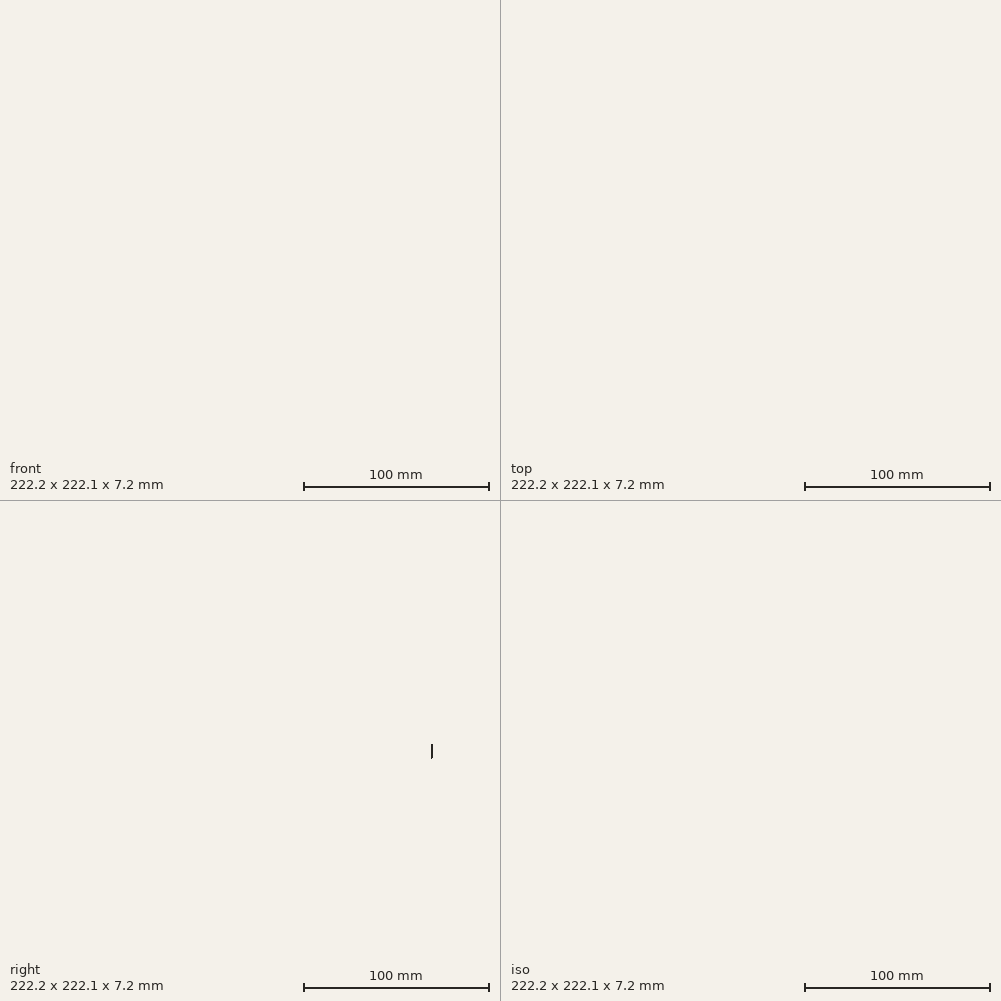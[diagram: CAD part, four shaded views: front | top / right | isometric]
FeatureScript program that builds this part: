
annotation { "Feature Type Name" : "Feature", "Feature Type Description" : "" }
export const myFeature = defineFeature(function(context is Context, id is Id, definition is map)
    precondition{}
    {
        {
            var Q0;
            Q0=qCreatedBy(makeId("Top.planeOp"),FACE);
            var sketch = newSketch(context, id + "F0", { "sketchPlane" : qUnion([Q0])});
            skCircle(sketch, "E0", {"center": v(0, 0) * mm, "radius": 101.6 * mm});
            skCircle(sketch, "E1", {"center": v(0, 0) * mm, "radius": 111.13 * mm});
            skSolve(sketch);
        }
        {
            var Q0;
            Q0=qSketchRegion(id+"F0",true);
            extrude(context, id + "F1", {"entities" : qUnion([Q0]), "depth" : 12.7 * mm});
        }
        {
            var Q0;
            Q0=makeQuery(id+"F1.opExtrude","CAP_FACE",FACE,{"disambiguationData":[OSD([sQuery(id+"F0.wireOp",EDGE,"E0"),sQuery(id+"F0.wireOp",EDGE,"E1")])],"isStart":false});
            var sketch = newSketch(context, id + "F2", { "sketchPlane" : qUnion([Q0])});
            skLineSegment(sketch, "E2", {"start": v(0, 0) * mm, "end": v(0, 111.13) * mm, "construction": true});
            skArc(sketch, "E3", {"start": v(1.28, 110.4) * mm, "mid": v(0.74, 110.93) * mm, "end": v(0, 111.12) * mm});
            skCircle(sketch, "E4", {"center": v(0, 0) * mm, "radius": 109.64 * mm, "construction": true});
            skArc(sketch, "E5", {"start": v(5.38, 111) * mm, "mid": v(4.64, 110.84) * mm, "end": v(4.08, 110.34) * mm});
            skArc(sketch, "E6", {"start": v(1.28, 110.4) * mm, "mid": v(2.66, 109.6) * mm, "end": v(4.08, 110.34) * mm});
            skLineSegment(sketch, "E7", {"start": v(5.31, 109.5) * mm, "end": v(5.38, 111) * mm, "construction": true});
            skCircle(sketch, "E8", {"center": v(0, 0) * mm, "radius": 129.3 * mm});
            skArc(sketch, "E9.1.0", {"start": v(-4.05, 110.33) * mm, "mid": v(-4.62, 110.84) * mm, "end": v(-5.37, 111) * mm});
            skArc(sketch, "E9.1.1", {"start": v(0.01, 111.12) * mm, "mid": v(-0.72, 110.93) * mm, "end": v(-1.26, 110.4) * mm});
            skArc(sketch, "E9.1.2", {"start": v(-4.05, 110.33) * mm, "mid": v(-2.64, 109.6) * mm, "end": v(-1.26, 110.4) * mm});
            skArc(sketch, "E9.2.0", {"start": v(-9.38, 110.01) * mm, "mid": v(-9.97, 110.48) * mm, "end": v(-10.73, 110.6) * mm});
            skArc(sketch, "E9.2.1", {"start": v(-5.35, 111) * mm, "mid": v(-6.08, 110.77) * mm, "end": v(-6.6, 110.22) * mm});
            skArc(sketch, "E9.2.2", {"start": v(-9.38, 110.01) * mm, "mid": v(-7.93, 109.35) * mm, "end": v(-6.6, 110.22) * mm});
            skArc(sketch, "E9.3.0", {"start": v(-14.68, 109.43) * mm, "mid": v(-15.3, 109.87) * mm, "end": v(-16.06, 109.96) * mm});
            skArc(sketch, "E9.3.1", {"start": v(-10.71, 110.6) * mm, "mid": v(-11.42, 110.35) * mm, "end": v(-11.9, 109.77) * mm});
            skArc(sketch, "E9.3.2", {"start": v(-14.68, 109.43) * mm, "mid": v(-13.2, 108.84) * mm, "end": v(-11.9, 109.77) * mm});
            skArc(sketch, "E9.4.0", {"start": v(-19.95, 108.6) * mm, "mid": v(-20.59, 109) * mm, "end": v(-21.35, 109.05) * mm});
            skArc(sketch, "E9.4.1", {"start": v(-16.04, 109.96) * mm, "mid": v(-16.74, 109.66) * mm, "end": v(-17.2, 109.06) * mm});
            skArc(sketch, "E9.4.2", {"start": v(-19.95, 108.6) * mm, "mid": v(-18.45, 108.07) * mm, "end": v(-17.2, 109.06) * mm});
            skArc(sketch, "E9.5.0", {"start": v(-25.17, 107.5) * mm, "mid": v(-25.83, 107.88) * mm, "end": v(-26.6, 107.9) * mm});
            skArc(sketch, "E9.5.1", {"start": v(-21.34, 109.06) * mm, "mid": v(-22.02, 108.73) * mm, "end": v(-22.45, 108.1) * mm});
            skArc(sketch, "E9.5.2", {"start": v(-25.17, 107.5) * mm, "mid": v(-23.65, 107.06) * mm, "end": v(-22.45, 108.1) * mm});
            skArc(sketch, "E9.6.0", {"start": v(-30.34, 106.16) * mm, "mid": v(-31.01, 106.51) * mm, "end": v(-31.78, 106.49) * mm});
            skArc(sketch, "E9.6.1", {"start": v(-26.58, 107.9) * mm, "mid": v(-27.24, 107.54) * mm, "end": v(-27.65, 106.9) * mm});
            skArc(sketch, "E9.6.2", {"start": v(-30.34, 106.16) * mm, "mid": v(-28.79, 105.79) * mm, "end": v(-27.65, 106.9) * mm});
            skArc(sketch, "E9.7.0", {"start": v(-35.43, 104.57) * mm, "mid": v(-36.12, 104.89) * mm, "end": v(-36.88, 104.83) * mm});
            skArc(sketch, "E9.7.1", {"start": v(-31.76, 106.49) * mm, "mid": v(-32.4, 106.1) * mm, "end": v(-32.78, 105.44) * mm});
            skArc(sketch, "E9.7.2", {"start": v(-35.43, 104.57) * mm, "mid": v(-33.87, 104.28) * mm, "end": v(-32.78, 105.44) * mm});
            skArc(sketch, "E9.8.0", {"start": v(-40.44, 102.74) * mm, "mid": v(-41.15, 103.02) * mm, "end": v(-41.9, 102.92) * mm});
            skArc(sketch, "E9.8.1", {"start": v(-36.87, 104.83) * mm, "mid": v(-37.5, 104.4) * mm, "end": v(-37.83, 103.73) * mm});
            skArc(sketch, "E9.8.2", {"start": v(-40.44, 102.74) * mm, "mid": v(-38.87, 102.52) * mm, "end": v(-37.83, 103.73) * mm});
            skArc(sketch, "E9.9.0", {"start": v(-45.36, 100.66) * mm, "mid": v(-46.08, 100.91) * mm, "end": v(-46.83, 100.78) * mm});
            skArc(sketch, "E9.9.1", {"start": v(-41.9, 102.93) * mm, "mid": v(-42.5, 102.47) * mm, "end": v(-42.8, 101.78) * mm});
            skArc(sketch, "E9.9.2", {"start": v(-45.36, 100.66) * mm, "mid": v(-43.77, 100.52) * mm, "end": v(-42.8, 101.78) * mm});
            skArc(sketch, "E9.10.0", {"start": v(-50.17, 98.35) * mm, "mid": v(-50.9, 98.57) * mm, "end": v(-51.64, 98.4) * mm});
            skArc(sketch, "E9.10.1", {"start": v(-46.82, 100.78) * mm, "mid": v(-47.4, 100.3) * mm, "end": v(-47.67, 99.6) * mm});
            skArc(sketch, "E9.10.2", {"start": v(-50.17, 98.35) * mm, "mid": v(-48.58, 98.29) * mm, "end": v(-47.67, 99.6) * mm});
            skArc(sketch, "E9.11.0", {"start": v(-54.86, 95.81) * mm, "mid": v(-55.6, 96) * mm, "end": v(-56.34, 95.79) * mm});
            skArc(sketch, "E9.11.1", {"start": v(-51.63, 98.4) * mm, "mid": v(-52.19, 97.9) * mm, "end": v(-52.42, 97.17) * mm});
            skArc(sketch, "E9.11.2", {"start": v(-54.86, 95.81) * mm, "mid": v(-53.27, 95.83) * mm, "end": v(-52.42, 97.17) * mm});
            skArc(sketch, "E9.12.0", {"start": v(-59.43, 93.05) * mm, "mid": v(-60.18, 93.2) * mm, "end": v(-60.9, 92.95) * mm});
            skArc(sketch, "E9.12.1", {"start": v(-56.32, 95.8) * mm, "mid": v(-56.86, 95.26) * mm, "end": v(-57.06, 94.53) * mm});
            skArc(sketch, "E9.12.2", {"start": v(-59.43, 93.05) * mm, "mid": v(-57.84, 93.14) * mm, "end": v(-57.06, 94.53) * mm});
            skArc(sketch, "E9.13.0", {"start": v(-63.85, 90.07) * mm, "mid": v(-64.6, 90.18) * mm, "end": v(-65.32, 89.9) * mm});
            skArc(sketch, "E9.13.1", {"start": v(-60.89, 92.96) * mm, "mid": v(-61.4, 92.4) * mm, "end": v(-61.56, 91.66) * mm});
            skArc(sketch, "E9.13.2", {"start": v(-63.85, 90.07) * mm, "mid": v(-62.27, 90.24) * mm, "end": v(-61.56, 91.66) * mm});
            skArc(sketch, "E9.14.0", {"start": v(-68.13, 86.88) * mm, "mid": v(-68.89, 86.95) * mm, "end": v(-69.58, 86.64) * mm});
            skArc(sketch, "E9.14.1", {"start": v(-65.3, 89.91) * mm, "mid": v(-65.79, 89.32) * mm, "end": v(-65.91, 88.58) * mm});
            skArc(sketch, "E9.14.2", {"start": v(-68.13, 86.88) * mm, "mid": v(-66.56, 87.12) * mm, "end": v(-65.91, 88.58) * mm});
            skArc(sketch, "E9.15.0", {"start": v(-72.25, 83.49) * mm, "mid": v(-73, 83.52) * mm, "end": v(-73.69, 83.18) * mm});
            skArc(sketch, "E9.15.1", {"start": v(-69.57, 86.65) * mm, "mid": v(-70.02, 86.04) * mm, "end": v(-70.12, 85.3) * mm});
            skArc(sketch, "E9.15.2", {"start": v(-72.25, 83.49) * mm, "mid": v(-70.69, 83.8) * mm, "end": v(-70.12, 85.3) * mm});
            skArc(sketch, "E9.16.0", {"start": v(-76.2, 79.9) * mm, "mid": v(-76.96, 79.9) * mm, "end": v(-77.62, 79.52) * mm});
            skArc(sketch, "E9.16.1", {"start": v(-73.68, 83.19) * mm, "mid": v(-74.1, 82.56) * mm, "end": v(-74.16, 81.8) * mm});
            skArc(sketch, "E9.16.2", {"start": v(-76.2, 79.9) * mm, "mid": v(-74.65, 80.3) * mm, "end": v(-74.16, 81.8) * mm});
            skArc(sketch, "E9.17.0", {"start": v(-79.97, 76.13) * mm, "mid": v(-80.73, 76.09) * mm, "end": v(-81.37, 75.68) * mm});
            skArc(sketch, "E9.17.1", {"start": v(-77.61, 79.53) * mm, "mid": v(-78, 78.88) * mm, "end": v(-78.02, 78.13) * mm});
            skArc(sketch, "E9.17.2", {"start": v(-79.97, 76.13) * mm, "mid": v(-78.45, 76.6) * mm, "end": v(-78.02, 78.13) * mm});
            skArc(sketch, "E9.18.0", {"start": v(-83.55, 72.17) * mm, "mid": v(-84.31, 72.1) * mm, "end": v(-84.93, 71.66) * mm});
            skArc(sketch, "E9.18.1", {"start": v(-81.36, 75.69) * mm, "mid": v(-81.72, 75.02) * mm, "end": v(-81.7, 74.27) * mm});
            skArc(sketch, "E9.18.2", {"start": v(-83.55, 72.17) * mm, "mid": v(-82.06, 72.71) * mm, "end": v(-81.7, 74.27) * mm});
            skArc(sketch, "E9.19.0", {"start": v(-86.94, 68.05) * mm, "mid": v(-87.7, 67.94) * mm, "end": v(-88.3, 67.47) * mm});
            skArc(sketch, "E9.19.1", {"start": v(-84.93, 71.67) * mm, "mid": v(-85.25, 70.99) * mm, "end": v(-85.2, 70.23) * mm});
            skArc(sketch, "E9.19.2", {"start": v(-86.94, 68.05) * mm, "mid": v(-85.47, 68.66) * mm, "end": v(-85.2, 70.23) * mm});
            skArc(sketch, "E9.20.0", {"start": v(-90.13, 63.77) * mm, "mid": v(-90.88, 63.62) * mm, "end": v(-91.45, 63.13) * mm});
            skArc(sketch, "E9.20.1", {"start": v(-88.29, 67.48) * mm, "mid": v(-88.58, 66.78) * mm, "end": v(-88.5, 66.03) * mm});
            skArc(sketch, "E9.20.2", {"start": v(-90.13, 63.77) * mm, "mid": v(-88.7, 64.45) * mm, "end": v(-88.5, 66.03) * mm});
            skArc(sketch, "E9.21.0", {"start": v(-93.1, 59.34) * mm, "mid": v(-93.84, 59.16) * mm, "end": v(-94.4, 58.63) * mm});
            skArc(sketch, "E9.21.1", {"start": v(-91.45, 63.14) * mm, "mid": v(-91.7, 62.43) * mm, "end": v(-91.58, 61.68) * mm});
            skArc(sketch, "E9.21.2", {"start": v(-93.1, 59.34) * mm, "mid": v(-91.7, 60.1) * mm, "end": v(-91.58, 61.68) * mm});
            skArc(sketch, "E9.22.0", {"start": v(-95.86, 54.78) * mm, "mid": v(-96.6, 54.56) * mm, "end": v(-97.12, 54) * mm});
            skArc(sketch, "E9.22.1", {"start": v(-94.39, 58.65) * mm, "mid": v(-94.61, 57.92) * mm, "end": v(-94.45, 57.18) * mm});
            skArc(sketch, "E9.22.2", {"start": v(-95.86, 54.78) * mm, "mid": v(-94.5, 55.6) * mm, "end": v(-94.45, 57.18) * mm});
            skArc(sketch, "E9.23.0", {"start": v(-98.4, 50.08) * mm, "mid": v(-99.12, 49.82) * mm, "end": v(-99.62, 49.25) * mm});
            skArc(sketch, "E9.23.1", {"start": v(-97.11, 54.02) * mm, "mid": v(-97.3, 53.28) * mm, "end": v(-97.1, 52.55) * mm});
            skArc(sketch, "E9.23.2", {"start": v(-98.4, 50.08) * mm, "mid": v(-97.07, 50.96) * mm, "end": v(-97.1, 52.55) * mm});
            skArc(sketch, "E9.24.0", {"start": v(-100.7, 45.27) * mm, "mid": v(-101.4, 44.98) * mm, "end": v(-101.88, 44.38) * mm});
            skArc(sketch, "E9.24.1", {"start": v(-99.6, 49.26) * mm, "mid": v(-99.76, 48.52) * mm, "end": v(-99.53, 47.8) * mm});
            skArc(sketch, "E9.24.2", {"start": v(-100.7, 45.27) * mm, "mid": v(-99.42, 46.21) * mm, "end": v(-99.53, 47.8) * mm});
            skArc(sketch, "E9.25.0", {"start": v(-102.77, 40.35) * mm, "mid": v(-103.46, 40.03) * mm, "end": v(-103.9, 39.4) * mm});
            skArc(sketch, "E9.25.1", {"start": v(-101.87, 44.4) * mm, "mid": v(-101.99, 43.64) * mm, "end": v(-101.72, 42.94) * mm});
            skArc(sketch, "E9.25.2", {"start": v(-102.77, 40.35) * mm, "mid": v(-101.54, 41.36) * mm, "end": v(-101.72, 42.94) * mm});
            skArc(sketch, "E9.26.0", {"start": v(-104.6, 35.34) * mm, "mid": v(-105.27, 34.98) * mm, "end": v(-105.69, 34.34) * mm});
            skArc(sketch, "E9.26.1", {"start": v(-103.9, 39.42) * mm, "mid": v(-103.98, 38.67) * mm, "end": v(-103.68, 37.97) * mm});
            skArc(sketch, "E9.26.2", {"start": v(-104.6, 35.34) * mm, "mid": v(-103.42, 36.4) * mm, "end": v(-103.68, 37.97) * mm});
            skArc(sketch, "E9.27.0", {"start": v(-106.19, 30.24) * mm, "mid": v(-106.84, 29.85) * mm, "end": v(-107.22, 29.2) * mm});
            skArc(sketch, "E9.27.1", {"start": v(-105.68, 34.35) * mm, "mid": v(-105.72, 33.6) * mm, "end": v(-105.4, 32.92) * mm});
            skArc(sketch, "E9.27.2", {"start": v(-106.19, 30.24) * mm, "mid": v(-105.06, 31.36) * mm, "end": v(-105.4, 32.92) * mm});
            skArc(sketch, "E9.28.0", {"start": v(-107.52, 25.08) * mm, "mid": v(-108.16, 24.66) * mm, "end": v(-108.5, 23.98) * mm});
            skArc(sketch, "E9.28.1", {"start": v(-107.22, 29.2) * mm, "mid": v(-107.22, 28.45) * mm, "end": v(-106.86, 27.79) * mm});
            skArc(sketch, "E9.28.2", {"start": v(-107.52, 25.08) * mm, "mid": v(-106.45, 26.25) * mm, "end": v(-106.86, 27.79) * mm});
            skArc(sketch, "E9.29.0", {"start": v(-108.6, 19.85) * mm, "mid": v(-109.22, 19.4) * mm, "end": v(-109.54, 18.7) * mm});
            skArc(sketch, "E9.29.1", {"start": v(-108.5, 24) * mm, "mid": v(-108.47, 23.24) * mm, "end": v(-108.08, 22.6) * mm});
            skArc(sketch, "E9.29.2", {"start": v(-108.6, 19.85) * mm, "mid": v(-107.6, 21.08) * mm, "end": v(-108.08, 22.6) * mm});
            skArc(sketch, "E9.30.0", {"start": v(-109.44, 14.58) * mm, "mid": v(-110.03, 14.1) * mm, "end": v(-110.31, 13.4) * mm});
            skArc(sketch, "E9.30.1", {"start": v(-109.54, 18.72) * mm, "mid": v(-109.47, 17.97) * mm, "end": v(-109.04, 17.35) * mm});
            skArc(sketch, "E9.30.2", {"start": v(-109.44, 14.58) * mm, "mid": v(-108.48, 15.85) * mm, "end": v(-109.04, 17.35) * mm});
            skArc(sketch, "E9.31.0", {"start": v(-110.02, 9.28) * mm, "mid": v(-110.59, 8.77) * mm, "end": v(-110.83, 8.05) * mm});
            skArc(sketch, "E9.31.1", {"start": v(-110.31, 13.4) * mm, "mid": v(-110.21, 12.66) * mm, "end": v(-109.75, 12.06) * mm});
            skArc(sketch, "E9.31.2", {"start": v(-110.02, 9.28) * mm, "mid": v(-109.12, 10.6) * mm, "end": v(-109.75, 12.06) * mm});
            skArc(sketch, "E9.32.0", {"start": v(-110.34, 3.95) * mm, "mid": v(-110.88, 3.42) * mm, "end": v(-111.1, 2.69) * mm});
            skArc(sketch, "E9.32.1", {"start": v(-110.83, 8.06) * mm, "mid": v(-110.7, 7.32) * mm, "end": v(-110.2, 6.74) * mm});
            skArc(sketch, "E9.32.2", {"start": v(-110.34, 3.95) * mm, "mid": v(-109.5, 5.31) * mm, "end": v(-110.2, 6.74) * mm});
            skArc(sketch, "E9.33.0", {"start": v(-110.4, -1.38) * mm, "mid": v(-110.92, -1.94) * mm, "end": v(-111.1, -2.69) * mm});
            skArc(sketch, "E9.33.1", {"start": v(-111.1, 2.7) * mm, "mid": v(-110.92, 1.96) * mm, "end": v(-110.4, 1.4) * mm});
            skArc(sketch, "E9.33.2", {"start": v(-110.4, -1.38) * mm, "mid": v(-109.64, 0.01) * mm, "end": v(-110.4, 1.4) * mm});
            skArc(sketch, "E9.34.0", {"start": v(-110.2, -6.72) * mm, "mid": v(-110.7, -7.3) * mm, "end": v(-110.83, -8.05) * mm});
            skArc(sketch, "E9.34.1", {"start": v(-111.1, -2.67) * mm, "mid": v(-110.88, -3.4) * mm, "end": v(-110.34, -3.93) * mm});
            skArc(sketch, "E9.34.2", {"start": v(-110.2, -6.72) * mm, "mid": v(-109.5, -5.28) * mm, "end": v(-110.34, -3.93) * mm});
            skArc(sketch, "E9.35.0", {"start": v(-109.75, -12.03) * mm, "mid": v(-110.21, -12.64) * mm, "end": v(-110.31, -13.4) * mm});
            skArc(sketch, "E9.35.1", {"start": v(-110.83, -8.03) * mm, "mid": v(-110.59, -8.75) * mm, "end": v(-110.02, -9.25) * mm});
            skArc(sketch, "E9.35.2", {"start": v(-109.75, -12.03) * mm, "mid": v(-109.13, -10.57) * mm, "end": v(-110.02, -9.25) * mm});
            skArc(sketch, "E9.36.0", {"start": v(-109.04, -17.32) * mm, "mid": v(-109.47, -17.95) * mm, "end": v(-109.54, -18.7) * mm});
            skArc(sketch, "E9.36.1", {"start": v(-110.32, -13.38) * mm, "mid": v(-110.04, -14.08) * mm, "end": v(-109.45, -14.56) * mm});
            skArc(sketch, "E9.36.2", {"start": v(-109.04, -17.32) * mm, "mid": v(-108.49, -15.83) * mm, "end": v(-109.45, -14.56) * mm});
            skArc(sketch, "E9.37.0", {"start": v(-108.08, -22.57) * mm, "mid": v(-108.48, -23.22) * mm, "end": v(-108.5, -23.98) * mm});
            skArc(sketch, "E9.37.1", {"start": v(-109.54, -18.7) * mm, "mid": v(-109.23, -19.38) * mm, "end": v(-108.62, -19.83) * mm});
            skArc(sketch, "E9.37.2", {"start": v(-108.08, -22.57) * mm, "mid": v(-107.6, -21.05) * mm, "end": v(-108.62, -19.83) * mm});
            skArc(sketch, "E9.38.0", {"start": v(-106.86, -27.76) * mm, "mid": v(-107.23, -28.43) * mm, "end": v(-107.22, -29.2) * mm});
            skArc(sketch, "E9.38.1", {"start": v(-108.51, -23.96) * mm, "mid": v(-108.16, -24.64) * mm, "end": v(-107.53, -25.05) * mm});
            skArc(sketch, "E9.38.2", {"start": v(-106.86, -27.76) * mm, "mid": v(-106.45, -26.23) * mm, "end": v(-107.53, -25.05) * mm});
            skArc(sketch, "E9.39.0", {"start": v(-105.4, -32.9) * mm, "mid": v(-105.73, -33.58) * mm, "end": v(-105.69, -34.34) * mm});
            skArc(sketch, "E9.39.1", {"start": v(-107.23, -29.18) * mm, "mid": v(-106.85, -29.84) * mm, "end": v(-106.2, -30.22) * mm});
            skArc(sketch, "E9.39.2", {"start": v(-105.4, -32.9) * mm, "mid": v(-105.06, -31.34) * mm, "end": v(-106.2, -30.22) * mm});
            skArc(sketch, "E9.40.0", {"start": v(-103.68, -37.95) * mm, "mid": v(-103.98, -38.65) * mm, "end": v(-103.9, -39.4) * mm});
            skArc(sketch, "E9.40.1", {"start": v(-105.7, -34.33) * mm, "mid": v(-105.28, -34.96) * mm, "end": v(-104.61, -35.32) * mm});
            skArc(sketch, "E9.40.2", {"start": v(-103.68, -37.95) * mm, "mid": v(-103.43, -36.38) * mm, "end": v(-104.61, -35.32) * mm});
            skArc(sketch, "E9.41.0", {"start": v(-101.73, -42.91) * mm, "mid": v(-102, -43.63) * mm, "end": v(-101.88, -44.38) * mm});
            skArc(sketch, "E9.41.1", {"start": v(-103.9, -39.4) * mm, "mid": v(-103.47, -40) * mm, "end": v(-102.78, -40.33) * mm});
            skArc(sketch, "E9.41.2", {"start": v(-101.73, -42.91) * mm, "mid": v(-101.55, -41.33) * mm, "end": v(-102.78, -40.33) * mm});
            skArc(sketch, "E9.42.0", {"start": v(-99.54, -47.78) * mm, "mid": v(-99.77, -48.5) * mm, "end": v(-99.62, -49.25) * mm});
            skArc(sketch, "E9.42.1", {"start": v(-101.88, -44.37) * mm, "mid": v(-101.42, -44.96) * mm, "end": v(-100.72, -45.25) * mm});
            skArc(sketch, "E9.42.2", {"start": v(-99.54, -47.78) * mm, "mid": v(-99.43, -46.19) * mm, "end": v(-100.72, -45.25) * mm});
            skArc(sketch, "E9.43.0", {"start": v(-97.11, -52.53) * mm, "mid": v(-97.3, -53.27) * mm, "end": v(-97.12, -54) * mm});
            skArc(sketch, "E9.43.1", {"start": v(-99.62, -49.24) * mm, "mid": v(-99.13, -49.8) * mm, "end": v(-98.41, -50.06) * mm});
            skArc(sketch, "E9.43.2", {"start": v(-97.11, -52.53) * mm, "mid": v(-97.08, -50.94) * mm, "end": v(-98.41, -50.06) * mm});
            skArc(sketch, "E9.44.0", {"start": v(-94.46, -57.16) * mm, "mid": v(-94.62, -57.9) * mm, "end": v(-94.4, -58.63) * mm});
            skArc(sketch, "E9.44.1", {"start": v(-97.13, -54) * mm, "mid": v(-96.6, -54.54) * mm, "end": v(-95.88, -54.76) * mm});
            skArc(sketch, "E9.44.2", {"start": v(-94.46, -57.16) * mm, "mid": v(-94.51, -55.57) * mm, "end": v(-95.88, -54.76) * mm});
            skArc(sketch, "E9.45.0", {"start": v(-91.59, -61.66) * mm, "mid": v(-91.71, -62.4) * mm, "end": v(-91.45, -63.13) * mm});
            skArc(sketch, "E9.45.1", {"start": v(-94.4, -58.62) * mm, "mid": v(-93.86, -59.14) * mm, "end": v(-93.12, -59.32) * mm});
            skArc(sketch, "E9.45.2", {"start": v(-91.59, -61.66) * mm, "mid": v(-91.72, -60.07) * mm, "end": v(-93.12, -59.32) * mm});
            skArc(sketch, "E9.46.0", {"start": v(-88.5, -66.01) * mm, "mid": v(-88.6, -66.77) * mm, "end": v(-88.3, -67.47) * mm});
            skArc(sketch, "E9.46.1", {"start": v(-91.46, -63.11) * mm, "mid": v(-90.89, -63.6) * mm, "end": v(-90.15, -63.75) * mm});
            skArc(sketch, "E9.46.2", {"start": v(-88.5, -66.01) * mm, "mid": v(-88.7, -64.43) * mm, "end": v(-90.15, -63.75) * mm});
            skArc(sketch, "E9.47.0", {"start": v(-85.21, -70.2) * mm, "mid": v(-85.26, -70.97) * mm, "end": v(-84.93, -71.66) * mm});
            skArc(sketch, "E9.47.1", {"start": v(-88.3, -67.46) * mm, "mid": v(-87.7, -67.92) * mm, "end": v(-86.96, -68.04) * mm});
            skArc(sketch, "E9.47.2", {"start": v(-85.21, -70.2) * mm, "mid": v(-85.49, -68.64) * mm, "end": v(-86.96, -68.04) * mm});
            skArc(sketch, "E9.48.0", {"start": v(-81.72, -74.24) * mm, "mid": v(-81.73, -75) * mm, "end": v(-81.37, -75.68) * mm});
            skArc(sketch, "E9.48.1", {"start": v(-84.94, -71.65) * mm, "mid": v(-84.33, -72.08) * mm, "end": v(-83.57, -72.16) * mm});
            skArc(sketch, "E9.48.2", {"start": v(-81.72, -74.24) * mm, "mid": v(-82.07, -72.7) * mm, "end": v(-83.57, -72.16) * mm});
            skArc(sketch, "E9.49.0", {"start": v(-78.04, -78.1) * mm, "mid": v(-78.01, -78.87) * mm, "end": v(-77.62, -79.52) * mm});
            skArc(sketch, "E9.49.1", {"start": v(-81.38, -75.67) * mm, "mid": v(-80.74, -76.07) * mm, "end": v(-79.99, -76.11) * mm});
            skArc(sketch, "E9.49.2", {"start": v(-78.04, -78.1) * mm, "mid": v(-78.47, -76.57) * mm, "end": v(-79.99, -76.11) * mm});
            skArc(sketch, "E9.50.0", {"start": v(-74.17, -81.78) * mm, "mid": v(-74.11, -82.54) * mm, "end": v(-73.69, -83.18) * mm});
            skArc(sketch, "E9.50.1", {"start": v(-77.63, -79.51) * mm, "mid": v(-76.97, -79.88) * mm, "end": v(-76.22, -79.89) * mm});
            skArc(sketch, "E9.50.2", {"start": v(-74.17, -81.78) * mm, "mid": v(-74.67, -80.27) * mm, "end": v(-76.22, -79.89) * mm});
            skArc(sketch, "E9.51.0", {"start": v(-70.13, -85.27) * mm, "mid": v(-70.04, -86.03) * mm, "end": v(-69.58, -86.64) * mm});
            skArc(sketch, "E9.51.1", {"start": v(-73.7, -83.17) * mm, "mid": v(-73.03, -83.51) * mm, "end": v(-72.27, -83.48) * mm});
            skArc(sketch, "E9.51.2", {"start": v(-70.13, -85.27) * mm, "mid": v(-70.7, -83.79) * mm, "end": v(-72.27, -83.48) * mm});
            skArc(sketch, "E9.52.0", {"start": v(-65.93, -88.56) * mm, "mid": v(-65.8, -89.31) * mm, "end": v(-65.32, -89.9) * mm});
            skArc(sketch, "E9.52.1", {"start": v(-69.6, -86.63) * mm, "mid": v(-68.9, -86.94) * mm, "end": v(-68.15, -86.87) * mm});
            skArc(sketch, "E9.52.2", {"start": v(-65.93, -88.56) * mm, "mid": v(-66.58, -87.1) * mm, "end": v(-68.15, -86.87) * mm});
            skArc(sketch, "E9.53.0", {"start": v(-61.58, -91.64) * mm, "mid": v(-61.4, -92.39) * mm, "end": v(-60.9, -92.95) * mm});
            skArc(sketch, "E9.53.1", {"start": v(-65.33, -89.9) * mm, "mid": v(-64.62, -90.17) * mm, "end": v(-63.88, -90.06) * mm});
            skArc(sketch, "E9.53.2", {"start": v(-61.58, -91.64) * mm, "mid": v(-62.3, -90.22) * mm, "end": v(-63.88, -90.06) * mm});
            skArc(sketch, "E9.54.0", {"start": v(-57.08, -94.51) * mm, "mid": v(-56.87, -95.25) * mm, "end": v(-56.34, -95.79) * mm});
            skArc(sketch, "E9.54.1", {"start": v(-60.9, -92.94) * mm, "mid": v(-60.2, -93.19) * mm, "end": v(-59.45, -93.04) * mm});
            skArc(sketch, "E9.54.2", {"start": v(-57.08, -94.51) * mm, "mid": v(-57.86, -93.13) * mm, "end": v(-59.45, -93.04) * mm});
            skArc(sketch, "E9.55.0", {"start": v(-52.44, -97.16) * mm, "mid": v(-52.2, -97.88) * mm, "end": v(-51.64, -98.4) * mm});
            skArc(sketch, "E9.55.1", {"start": v(-56.35, -95.78) * mm, "mid": v(-55.62, -95.98) * mm, "end": v(-54.88, -95.8) * mm});
            skArc(sketch, "E9.55.2", {"start": v(-52.44, -97.16) * mm, "mid": v(-53.3, -95.81) * mm, "end": v(-54.88, -95.8) * mm});
            skArc(sketch, "E9.56.0", {"start": v(-47.69, -99.58) * mm, "mid": v(-47.42, -100.3) * mm, "end": v(-46.83, -100.78) * mm});
            skArc(sketch, "E9.56.1", {"start": v(-51.66, -98.39) * mm, "mid": v(-50.92, -98.56) * mm, "end": v(-50.2, -98.34) * mm});
            skArc(sketch, "E9.56.2", {"start": v(-47.69, -99.58) * mm, "mid": v(-48.6, -98.28) * mm, "end": v(-50.2, -98.34) * mm});
            skArc(sketch, "E9.57.0", {"start": v(-42.82, -101.77) * mm, "mid": v(-42.51, -102.46) * mm, "end": v(-41.9, -102.92) * mm});
            skArc(sketch, "E9.57.1", {"start": v(-46.84, -100.77) * mm, "mid": v(-46.1, -100.9) * mm, "end": v(-45.38, -100.65) * mm});
            skArc(sketch, "E9.57.2", {"start": v(-42.82, -101.77) * mm, "mid": v(-43.8, -100.5) * mm, "end": v(-45.38, -100.65) * mm});
            skArc(sketch, "E9.58.0", {"start": v(-37.85, -103.72) * mm, "mid": v(-37.51, -104.4) * mm, "end": v(-36.88, -104.83) * mm});
            skArc(sketch, "E9.58.1", {"start": v(-41.92, -102.92) * mm, "mid": v(-41.17, -103.01) * mm, "end": v(-40.47, -102.73) * mm});
            skArc(sketch, "E9.58.2", {"start": v(-37.85, -103.72) * mm, "mid": v(-38.9, -102.5) * mm, "end": v(-40.47, -102.73) * mm});
            skArc(sketch, "E9.59.0", {"start": v(-32.8, -105.42) * mm, "mid": v(-32.43, -106.09) * mm, "end": v(-31.78, -106.49) * mm});
            skArc(sketch, "E9.59.1", {"start": v(-36.9, -104.82) * mm, "mid": v(-36.14, -104.88) * mm, "end": v(-35.46, -104.56) * mm});
            skArc(sketch, "E9.59.2", {"start": v(-32.8, -105.42) * mm, "mid": v(-33.9, -104.27) * mm, "end": v(-35.46, -104.56) * mm});
            skArc(sketch, "E9.60.0", {"start": v(-27.67, -106.89) * mm, "mid": v(-27.26, -107.53) * mm, "end": v(-26.6, -107.9) * mm});
            skArc(sketch, "E9.60.1", {"start": v(-31.79, -106.48) * mm, "mid": v(-31.03, -106.5) * mm, "end": v(-30.36, -106.16) * mm});
            skArc(sketch, "E9.60.2", {"start": v(-27.67, -106.89) * mm, "mid": v(-28.82, -105.78) * mm, "end": v(-30.36, -106.16) * mm});
            skArc(sketch, "E9.61.0", {"start": v(-22.47, -108.1) * mm, "mid": v(-22.04, -108.72) * mm, "end": v(-21.35, -109.05) * mm});
            skArc(sketch, "E9.61.1", {"start": v(-26.6, -107.9) * mm, "mid": v(-25.85, -107.88) * mm, "end": v(-25.2, -107.5) * mm});
            skArc(sketch, "E9.61.2", {"start": v(-22.47, -108.1) * mm, "mid": v(-23.67, -107.05) * mm, "end": v(-25.2, -107.5) * mm});
            skArc(sketch, "E9.62.0", {"start": v(-17.22, -109.06) * mm, "mid": v(-16.76, -109.66) * mm, "end": v(-16.06, -109.96) * mm});
            skArc(sketch, "E9.62.1", {"start": v(-21.36, -109.05) * mm, "mid": v(-20.6, -109) * mm, "end": v(-19.98, -108.6) * mm});
            skArc(sketch, "E9.62.2", {"start": v(-17.22, -109.06) * mm, "mid": v(-18.47, -108.07) * mm, "end": v(-19.98, -108.6) * mm});
            skArc(sketch, "E9.63.0", {"start": v(-11.93, -109.76) * mm, "mid": v(-11.44, -110.34) * mm, "end": v(-10.73, -110.6) * mm});
            skArc(sketch, "E9.63.1", {"start": v(-16.07, -109.96) * mm, "mid": v(-15.32, -109.87) * mm, "end": v(-14.7, -109.43) * mm});
            skArc(sketch, "E9.63.2", {"start": v(-11.93, -109.76) * mm, "mid": v(-13.23, -108.84) * mm, "end": v(-14.7, -109.43) * mm});
            skArc(sketch, "E9.64.0", {"start": v(-6.62, -110.21) * mm, "mid": v(-6.1, -110.77) * mm, "end": v(-5.37, -111) * mm});
            skArc(sketch, "E9.64.1", {"start": v(-10.74, -110.6) * mm, "mid": v(-10, -110.48) * mm, "end": v(-9.4, -110.01) * mm});
            skArc(sketch, "E9.64.2", {"start": v(-6.62, -110.21) * mm, "mid": v(-7.95, -109.35) * mm, "end": v(-9.4, -110.01) * mm});
            skArc(sketch, "E9.65.0", {"start": v(-1.28, -110.4) * mm, "mid": v(-0.74, -110.93) * mm, "end": v(0, -111.12) * mm});
            skArc(sketch, "E9.65.1", {"start": v(-5.38, -111) * mm, "mid": v(-4.64, -110.84) * mm, "end": v(-4.08, -110.34) * mm});
            skArc(sketch, "E9.65.2", {"start": v(-1.28, -110.4) * mm, "mid": v(-2.66, -109.6) * mm, "end": v(-4.08, -110.34) * mm});
            skArc(sketch, "E9.66.0", {"start": v(4.05, -110.33) * mm, "mid": v(4.62, -110.84) * mm, "end": v(5.37, -111) * mm});
            skArc(sketch, "E9.66.1", {"start": v(-0.01, -111.12) * mm, "mid": v(0.72, -110.93) * mm, "end": v(1.26, -110.4) * mm});
            skArc(sketch, "E9.66.2", {"start": v(4.05, -110.33) * mm, "mid": v(2.64, -109.6) * mm, "end": v(1.26, -110.4) * mm});
            skArc(sketch, "E9.67.0", {"start": v(9.38, -110.01) * mm, "mid": v(9.97, -110.48) * mm, "end": v(10.73, -110.6) * mm});
            skArc(sketch, "E9.67.1", {"start": v(5.35, -111) * mm, "mid": v(6.08, -110.77) * mm, "end": v(6.6, -110.22) * mm});
            skArc(sketch, "E9.67.2", {"start": v(9.38, -110.01) * mm, "mid": v(7.93, -109.35) * mm, "end": v(6.6, -110.22) * mm});
            skArc(sketch, "E9.68.0", {"start": v(14.68, -109.43) * mm, "mid": v(15.3, -109.87) * mm, "end": v(16.06, -109.96) * mm});
            skArc(sketch, "E9.68.1", {"start": v(10.71, -110.6) * mm, "mid": v(11.42, -110.35) * mm, "end": v(11.9, -109.77) * mm});
            skArc(sketch, "E9.68.2", {"start": v(14.68, -109.43) * mm, "mid": v(13.2, -108.84) * mm, "end": v(11.9, -109.77) * mm});
            skArc(sketch, "E9.69.0", {"start": v(19.95, -108.6) * mm, "mid": v(20.59, -109) * mm, "end": v(21.35, -109.05) * mm});
            skArc(sketch, "E9.69.1", {"start": v(16.04, -109.96) * mm, "mid": v(16.74, -109.66) * mm, "end": v(17.2, -109.06) * mm});
            skArc(sketch, "E9.69.2", {"start": v(19.95, -108.6) * mm, "mid": v(18.45, -108.07) * mm, "end": v(17.2, -109.06) * mm});
            skArc(sketch, "E9.70.0", {"start": v(25.17, -107.5) * mm, "mid": v(25.83, -107.88) * mm, "end": v(26.6, -107.9) * mm});
            skArc(sketch, "E9.70.1", {"start": v(21.34, -109.06) * mm, "mid": v(22.02, -108.73) * mm, "end": v(22.45, -108.1) * mm});
            skArc(sketch, "E9.70.2", {"start": v(25.17, -107.5) * mm, "mid": v(23.65, -107.06) * mm, "end": v(22.45, -108.1) * mm});
            skArc(sketch, "E9.71.0", {"start": v(30.34, -106.16) * mm, "mid": v(31.01, -106.51) * mm, "end": v(31.78, -106.49) * mm});
            skArc(sketch, "E9.71.1", {"start": v(26.58, -107.9) * mm, "mid": v(27.24, -107.54) * mm, "end": v(27.65, -106.9) * mm});
            skArc(sketch, "E9.71.2", {"start": v(30.34, -106.16) * mm, "mid": v(28.79, -105.79) * mm, "end": v(27.65, -106.9) * mm});
            skArc(sketch, "E9.72.0", {"start": v(35.43, -104.57) * mm, "mid": v(36.12, -104.89) * mm, "end": v(36.88, -104.83) * mm});
            skArc(sketch, "E9.72.1", {"start": v(31.76, -106.49) * mm, "mid": v(32.4, -106.1) * mm, "end": v(32.78, -105.44) * mm});
            skArc(sketch, "E9.72.2", {"start": v(35.43, -104.57) * mm, "mid": v(33.87, -104.28) * mm, "end": v(32.78, -105.44) * mm});
            skArc(sketch, "E9.73.0", {"start": v(40.44, -102.74) * mm, "mid": v(41.15, -103.02) * mm, "end": v(41.9, -102.92) * mm});
            skArc(sketch, "E9.73.1", {"start": v(36.87, -104.83) * mm, "mid": v(37.5, -104.4) * mm, "end": v(37.83, -103.73) * mm});
            skArc(sketch, "E9.73.2", {"start": v(40.44, -102.74) * mm, "mid": v(38.87, -102.52) * mm, "end": v(37.83, -103.73) * mm});
            skArc(sketch, "E9.74.0", {"start": v(45.36, -100.66) * mm, "mid": v(46.08, -100.91) * mm, "end": v(46.83, -100.78) * mm});
            skArc(sketch, "E9.74.1", {"start": v(41.9, -102.93) * mm, "mid": v(42.5, -102.47) * mm, "end": v(42.8, -101.78) * mm});
            skArc(sketch, "E9.74.2", {"start": v(45.36, -100.66) * mm, "mid": v(43.77, -100.52) * mm, "end": v(42.8, -101.78) * mm});
            skArc(sketch, "E9.75.0", {"start": v(50.17, -98.35) * mm, "mid": v(50.9, -98.57) * mm, "end": v(51.64, -98.4) * mm});
            skArc(sketch, "E9.75.1", {"start": v(46.82, -100.78) * mm, "mid": v(47.4, -100.3) * mm, "end": v(47.67, -99.6) * mm});
            skArc(sketch, "E9.75.2", {"start": v(50.17, -98.35) * mm, "mid": v(48.58, -98.29) * mm, "end": v(47.67, -99.6) * mm});
            skArc(sketch, "E9.76.0", {"start": v(54.86, -95.81) * mm, "mid": v(55.6, -96) * mm, "end": v(56.34, -95.79) * mm});
            skArc(sketch, "E9.76.1", {"start": v(51.63, -98.4) * mm, "mid": v(52.19, -97.9) * mm, "end": v(52.42, -97.17) * mm});
            skArc(sketch, "E9.76.2", {"start": v(54.86, -95.81) * mm, "mid": v(53.27, -95.83) * mm, "end": v(52.42, -97.17) * mm});
            skArc(sketch, "E9.77.0", {"start": v(59.43, -93.05) * mm, "mid": v(60.18, -93.2) * mm, "end": v(60.9, -92.95) * mm});
            skArc(sketch, "E9.77.1", {"start": v(56.32, -95.8) * mm, "mid": v(56.86, -95.26) * mm, "end": v(57.06, -94.53) * mm});
            skArc(sketch, "E9.77.2", {"start": v(59.43, -93.05) * mm, "mid": v(57.84, -93.14) * mm, "end": v(57.06, -94.53) * mm});
            skArc(sketch, "E9.78.0", {"start": v(63.85, -90.07) * mm, "mid": v(64.6, -90.18) * mm, "end": v(65.32, -89.9) * mm});
            skArc(sketch, "E9.78.1", {"start": v(60.89, -92.96) * mm, "mid": v(61.4, -92.4) * mm, "end": v(61.56, -91.66) * mm});
            skArc(sketch, "E9.78.2", {"start": v(63.85, -90.07) * mm, "mid": v(62.27, -90.24) * mm, "end": v(61.56, -91.66) * mm});
            skArc(sketch, "E9.79.0", {"start": v(68.13, -86.88) * mm, "mid": v(68.89, -86.95) * mm, "end": v(69.58, -86.64) * mm});
            skArc(sketch, "E9.79.1", {"start": v(65.3, -89.91) * mm, "mid": v(65.79, -89.32) * mm, "end": v(65.91, -88.58) * mm});
            skArc(sketch, "E9.79.2", {"start": v(68.13, -86.88) * mm, "mid": v(66.56, -87.12) * mm, "end": v(65.91, -88.58) * mm});
            skArc(sketch, "E9.80.0", {"start": v(72.25, -83.49) * mm, "mid": v(73, -83.52) * mm, "end": v(73.69, -83.18) * mm});
            skArc(sketch, "E9.80.1", {"start": v(69.57, -86.65) * mm, "mid": v(70.02, -86.04) * mm, "end": v(70.12, -85.3) * mm});
            skArc(sketch, "E9.80.2", {"start": v(72.25, -83.49) * mm, "mid": v(70.69, -83.8) * mm, "end": v(70.12, -85.3) * mm});
            skArc(sketch, "E9.81.0", {"start": v(76.2, -79.9) * mm, "mid": v(76.96, -79.9) * mm, "end": v(77.62, -79.52) * mm});
            skArc(sketch, "E9.81.1", {"start": v(73.68, -83.19) * mm, "mid": v(74.1, -82.56) * mm, "end": v(74.16, -81.8) * mm});
            skArc(sketch, "E9.81.2", {"start": v(76.2, -79.9) * mm, "mid": v(74.65, -80.3) * mm, "end": v(74.16, -81.8) * mm});
            skArc(sketch, "E9.82.0", {"start": v(79.97, -76.13) * mm, "mid": v(80.73, -76.09) * mm, "end": v(81.37, -75.68) * mm});
            skArc(sketch, "E9.82.1", {"start": v(77.61, -79.53) * mm, "mid": v(78, -78.88) * mm, "end": v(78.02, -78.13) * mm});
            skArc(sketch, "E9.82.2", {"start": v(79.97, -76.13) * mm, "mid": v(78.45, -76.6) * mm, "end": v(78.02, -78.13) * mm});
            skArc(sketch, "E9.83.0", {"start": v(83.55, -72.17) * mm, "mid": v(84.31, -72.1) * mm, "end": v(84.93, -71.66) * mm});
            skArc(sketch, "E9.83.1", {"start": v(81.36, -75.69) * mm, "mid": v(81.72, -75.02) * mm, "end": v(81.7, -74.27) * mm});
            skArc(sketch, "E9.83.2", {"start": v(83.55, -72.17) * mm, "mid": v(82.06, -72.71) * mm, "end": v(81.7, -74.27) * mm});
            skArc(sketch, "E9.84.0", {"start": v(86.94, -68.05) * mm, "mid": v(87.7, -67.94) * mm, "end": v(88.3, -67.47) * mm});
            skArc(sketch, "E9.84.1", {"start": v(84.93, -71.67) * mm, "mid": v(85.25, -70.99) * mm, "end": v(85.2, -70.23) * mm});
            skArc(sketch, "E9.84.2", {"start": v(86.94, -68.05) * mm, "mid": v(85.47, -68.66) * mm, "end": v(85.2, -70.23) * mm});
            skArc(sketch, "E9.85.0", {"start": v(90.13, -63.77) * mm, "mid": v(90.88, -63.62) * mm, "end": v(91.45, -63.13) * mm});
            skArc(sketch, "E9.85.1", {"start": v(88.29, -67.48) * mm, "mid": v(88.58, -66.78) * mm, "end": v(88.5, -66.03) * mm});
            skArc(sketch, "E9.85.2", {"start": v(90.13, -63.77) * mm, "mid": v(88.7, -64.45) * mm, "end": v(88.5, -66.03) * mm});
            skArc(sketch, "E9.86.0", {"start": v(93.1, -59.34) * mm, "mid": v(93.84, -59.16) * mm, "end": v(94.4, -58.63) * mm});
            skArc(sketch, "E9.86.1", {"start": v(91.45, -63.14) * mm, "mid": v(91.7, -62.43) * mm, "end": v(91.58, -61.68) * mm});
            skArc(sketch, "E9.86.2", {"start": v(93.1, -59.34) * mm, "mid": v(91.7, -60.1) * mm, "end": v(91.58, -61.68) * mm});
            skArc(sketch, "E9.87.0", {"start": v(95.86, -54.78) * mm, "mid": v(96.6, -54.56) * mm, "end": v(97.12, -54) * mm});
            skArc(sketch, "E9.87.1", {"start": v(94.39, -58.65) * mm, "mid": v(94.61, -57.92) * mm, "end": v(94.45, -57.18) * mm});
            skArc(sketch, "E9.87.2", {"start": v(95.86, -54.78) * mm, "mid": v(94.5, -55.6) * mm, "end": v(94.45, -57.18) * mm});
            skArc(sketch, "E9.88.0", {"start": v(98.4, -50.08) * mm, "mid": v(99.12, -49.82) * mm, "end": v(99.62, -49.25) * mm});
            skArc(sketch, "E9.88.1", {"start": v(97.11, -54.02) * mm, "mid": v(97.3, -53.28) * mm, "end": v(97.1, -52.55) * mm});
            skArc(sketch, "E9.88.2", {"start": v(98.4, -50.08) * mm, "mid": v(97.07, -50.96) * mm, "end": v(97.1, -52.55) * mm});
            skArc(sketch, "E9.89.0", {"start": v(100.7, -45.27) * mm, "mid": v(101.4, -44.98) * mm, "end": v(101.88, -44.38) * mm});
            skArc(sketch, "E9.89.1", {"start": v(99.6, -49.26) * mm, "mid": v(99.76, -48.52) * mm, "end": v(99.53, -47.8) * mm});
            skArc(sketch, "E9.89.2", {"start": v(100.7, -45.27) * mm, "mid": v(99.42, -46.21) * mm, "end": v(99.53, -47.8) * mm});
            skArc(sketch, "E9.90.0", {"start": v(102.77, -40.35) * mm, "mid": v(103.46, -40.03) * mm, "end": v(103.9, -39.4) * mm});
            skArc(sketch, "E9.90.1", {"start": v(101.87, -44.4) * mm, "mid": v(101.99, -43.64) * mm, "end": v(101.72, -42.94) * mm});
            skArc(sketch, "E9.90.2", {"start": v(102.77, -40.35) * mm, "mid": v(101.54, -41.36) * mm, "end": v(101.72, -42.94) * mm});
            skArc(sketch, "E9.91.0", {"start": v(104.6, -35.34) * mm, "mid": v(105.27, -34.98) * mm, "end": v(105.69, -34.34) * mm});
            skArc(sketch, "E9.91.1", {"start": v(103.9, -39.42) * mm, "mid": v(103.98, -38.67) * mm, "end": v(103.68, -37.97) * mm});
            skArc(sketch, "E9.91.2", {"start": v(104.6, -35.34) * mm, "mid": v(103.42, -36.4) * mm, "end": v(103.68, -37.97) * mm});
            skArc(sketch, "E9.92.0", {"start": v(106.19, -30.24) * mm, "mid": v(106.84, -29.85) * mm, "end": v(107.22, -29.2) * mm});
            skArc(sketch, "E9.92.1", {"start": v(105.68, -34.35) * mm, "mid": v(105.72, -33.6) * mm, "end": v(105.4, -32.92) * mm});
            skArc(sketch, "E9.92.2", {"start": v(106.19, -30.24) * mm, "mid": v(105.06, -31.36) * mm, "end": v(105.4, -32.92) * mm});
            skArc(sketch, "E9.93.0", {"start": v(107.52, -25.08) * mm, "mid": v(108.16, -24.66) * mm, "end": v(108.5, -23.98) * mm});
            skArc(sketch, "E9.93.1", {"start": v(107.22, -29.2) * mm, "mid": v(107.22, -28.45) * mm, "end": v(106.86, -27.79) * mm});
            skArc(sketch, "E9.93.2", {"start": v(107.52, -25.08) * mm, "mid": v(106.45, -26.25) * mm, "end": v(106.86, -27.79) * mm});
            skArc(sketch, "E9.94.0", {"start": v(108.6, -19.85) * mm, "mid": v(109.22, -19.4) * mm, "end": v(109.54, -18.7) * mm});
            skArc(sketch, "E9.94.1", {"start": v(108.5, -24) * mm, "mid": v(108.47, -23.24) * mm, "end": v(108.08, -22.6) * mm});
            skArc(sketch, "E9.94.2", {"start": v(108.6, -19.85) * mm, "mid": v(107.6, -21.08) * mm, "end": v(108.08, -22.6) * mm});
            skArc(sketch, "E9.95.0", {"start": v(109.44, -14.58) * mm, "mid": v(110.03, -14.1) * mm, "end": v(110.31, -13.4) * mm});
            skArc(sketch, "E9.95.1", {"start": v(109.54, -18.72) * mm, "mid": v(109.47, -17.97) * mm, "end": v(109.04, -17.35) * mm});
            skArc(sketch, "E9.95.2", {"start": v(109.44, -14.58) * mm, "mid": v(108.48, -15.85) * mm, "end": v(109.04, -17.35) * mm});
            skArc(sketch, "E9.96.0", {"start": v(110.02, -9.28) * mm, "mid": v(110.59, -8.77) * mm, "end": v(110.83, -8.05) * mm});
            skArc(sketch, "E9.96.1", {"start": v(110.31, -13.4) * mm, "mid": v(110.21, -12.66) * mm, "end": v(109.75, -12.06) * mm});
            skArc(sketch, "E9.96.2", {"start": v(110.02, -9.28) * mm, "mid": v(109.12, -10.6) * mm, "end": v(109.75, -12.06) * mm});
            skArc(sketch, "E9.97.0", {"start": v(110.34, -3.95) * mm, "mid": v(110.88, -3.42) * mm, "end": v(111.1, -2.69) * mm});
            skArc(sketch, "E9.97.1", {"start": v(110.83, -8.06) * mm, "mid": v(110.7, -7.32) * mm, "end": v(110.2, -6.74) * mm});
            skArc(sketch, "E9.97.2", {"start": v(110.34, -3.95) * mm, "mid": v(109.5, -5.31) * mm, "end": v(110.2, -6.74) * mm});
            skArc(sketch, "E9.98.0", {"start": v(110.4, 1.38) * mm, "mid": v(110.92, 1.94) * mm, "end": v(111.1, 2.69) * mm});
            skArc(sketch, "E9.98.1", {"start": v(111.1, -2.7) * mm, "mid": v(110.92, -1.96) * mm, "end": v(110.4, -1.4) * mm});
            skArc(sketch, "E9.98.2", {"start": v(110.4, 1.38) * mm, "mid": v(109.64, -0.01) * mm, "end": v(110.4, -1.4) * mm});
            skArc(sketch, "E9.99.0", {"start": v(110.2, 6.72) * mm, "mid": v(110.7, 7.3) * mm, "end": v(110.83, 8.05) * mm});
            skArc(sketch, "E9.99.1", {"start": v(111.1, 2.67) * mm, "mid": v(110.88, 3.4) * mm, "end": v(110.34, 3.93) * mm});
            skArc(sketch, "E9.99.2", {"start": v(110.2, 6.72) * mm, "mid": v(109.5, 5.28) * mm, "end": v(110.34, 3.93) * mm});
            skArc(sketch, "E9.100.0", {"start": v(109.75, 12.03) * mm, "mid": v(110.21, 12.64) * mm, "end": v(110.31, 13.4) * mm});
            skArc(sketch, "E9.100.1", {"start": v(110.83, 8.03) * mm, "mid": v(110.59, 8.75) * mm, "end": v(110.02, 9.25) * mm});
            skArc(sketch, "E9.100.2", {"start": v(109.75, 12.03) * mm, "mid": v(109.13, 10.57) * mm, "end": v(110.02, 9.25) * mm});
            skArc(sketch, "E9.101.0", {"start": v(109.04, 17.32) * mm, "mid": v(109.47, 17.95) * mm, "end": v(109.54, 18.7) * mm});
            skArc(sketch, "E9.101.1", {"start": v(110.32, 13.38) * mm, "mid": v(110.04, 14.08) * mm, "end": v(109.45, 14.56) * mm});
            skArc(sketch, "E9.101.2", {"start": v(109.04, 17.32) * mm, "mid": v(108.49, 15.83) * mm, "end": v(109.45, 14.56) * mm});
            skArc(sketch, "E9.102.0", {"start": v(108.08, 22.57) * mm, "mid": v(108.48, 23.22) * mm, "end": v(108.5, 23.98) * mm});
            skArc(sketch, "E9.102.1", {"start": v(109.54, 18.7) * mm, "mid": v(109.23, 19.38) * mm, "end": v(108.62, 19.83) * mm});
            skArc(sketch, "E9.102.2", {"start": v(108.08, 22.57) * mm, "mid": v(107.6, 21.05) * mm, "end": v(108.62, 19.83) * mm});
            skArc(sketch, "E9.103.0", {"start": v(106.86, 27.76) * mm, "mid": v(107.23, 28.43) * mm, "end": v(107.22, 29.2) * mm});
            skArc(sketch, "E9.103.1", {"start": v(108.51, 23.96) * mm, "mid": v(108.16, 24.64) * mm, "end": v(107.53, 25.05) * mm});
            skArc(sketch, "E9.103.2", {"start": v(106.86, 27.76) * mm, "mid": v(106.45, 26.23) * mm, "end": v(107.53, 25.05) * mm});
            skArc(sketch, "E9.104.0", {"start": v(105.4, 32.9) * mm, "mid": v(105.73, 33.58) * mm, "end": v(105.69, 34.34) * mm});
            skArc(sketch, "E9.104.1", {"start": v(107.23, 29.18) * mm, "mid": v(106.85, 29.84) * mm, "end": v(106.2, 30.22) * mm});
            skArc(sketch, "E9.104.2", {"start": v(105.4, 32.9) * mm, "mid": v(105.06, 31.34) * mm, "end": v(106.2, 30.22) * mm});
            skArc(sketch, "E9.105.0", {"start": v(103.68, 37.95) * mm, "mid": v(103.98, 38.65) * mm, "end": v(103.9, 39.4) * mm});
            skArc(sketch, "E9.105.1", {"start": v(105.7, 34.33) * mm, "mid": v(105.28, 34.96) * mm, "end": v(104.61, 35.32) * mm});
            skArc(sketch, "E9.105.2", {"start": v(103.68, 37.95) * mm, "mid": v(103.43, 36.38) * mm, "end": v(104.61, 35.32) * mm});
            skArc(sketch, "E9.106.0", {"start": v(101.73, 42.91) * mm, "mid": v(102, 43.63) * mm, "end": v(101.88, 44.38) * mm});
            skArc(sketch, "E9.106.1", {"start": v(103.9, 39.4) * mm, "mid": v(103.47, 40) * mm, "end": v(102.78, 40.33) * mm});
            skArc(sketch, "E9.106.2", {"start": v(101.73, 42.91) * mm, "mid": v(101.55, 41.33) * mm, "end": v(102.78, 40.33) * mm});
            skArc(sketch, "E9.107.0", {"start": v(99.54, 47.78) * mm, "mid": v(99.77, 48.5) * mm, "end": v(99.62, 49.25) * mm});
            skArc(sketch, "E9.107.1", {"start": v(101.88, 44.37) * mm, "mid": v(101.42, 44.96) * mm, "end": v(100.72, 45.25) * mm});
            skArc(sketch, "E9.107.2", {"start": v(99.54, 47.78) * mm, "mid": v(99.43, 46.19) * mm, "end": v(100.72, 45.25) * mm});
            skArc(sketch, "E9.108.0", {"start": v(97.11, 52.53) * mm, "mid": v(97.3, 53.27) * mm, "end": v(97.12, 54) * mm});
            skArc(sketch, "E9.108.1", {"start": v(99.62, 49.24) * mm, "mid": v(99.13, 49.8) * mm, "end": v(98.41, 50.06) * mm});
            skArc(sketch, "E9.108.2", {"start": v(97.11, 52.53) * mm, "mid": v(97.08, 50.94) * mm, "end": v(98.41, 50.06) * mm});
            skArc(sketch, "E9.109.0", {"start": v(94.46, 57.16) * mm, "mid": v(94.62, 57.9) * mm, "end": v(94.4, 58.63) * mm});
            skArc(sketch, "E9.109.1", {"start": v(97.13, 54) * mm, "mid": v(96.6, 54.54) * mm, "end": v(95.88, 54.76) * mm});
            skArc(sketch, "E9.109.2", {"start": v(94.46, 57.16) * mm, "mid": v(94.51, 55.57) * mm, "end": v(95.88, 54.76) * mm});
            skArc(sketch, "E9.110.0", {"start": v(91.59, 61.66) * mm, "mid": v(91.71, 62.4) * mm, "end": v(91.45, 63.13) * mm});
            skArc(sketch, "E9.110.1", {"start": v(94.4, 58.62) * mm, "mid": v(93.86, 59.14) * mm, "end": v(93.12, 59.32) * mm});
            skArc(sketch, "E9.110.2", {"start": v(91.59, 61.66) * mm, "mid": v(91.72, 60.07) * mm, "end": v(93.12, 59.32) * mm});
            skArc(sketch, "E9.111.0", {"start": v(88.5, 66.01) * mm, "mid": v(88.6, 66.77) * mm, "end": v(88.3, 67.47) * mm});
            skArc(sketch, "E9.111.1", {"start": v(91.46, 63.11) * mm, "mid": v(90.89, 63.6) * mm, "end": v(90.15, 63.75) * mm});
            skArc(sketch, "E9.111.2", {"start": v(88.5, 66.01) * mm, "mid": v(88.7, 64.43) * mm, "end": v(90.15, 63.75) * mm});
            skArc(sketch, "E9.112.0", {"start": v(85.21, 70.2) * mm, "mid": v(85.26, 70.97) * mm, "end": v(84.93, 71.66) * mm});
            skArc(sketch, "E9.112.1", {"start": v(88.3, 67.46) * mm, "mid": v(87.7, 67.92) * mm, "end": v(86.96, 68.04) * mm});
            skArc(sketch, "E9.112.2", {"start": v(85.21, 70.2) * mm, "mid": v(85.49, 68.64) * mm, "end": v(86.96, 68.04) * mm});
            skArc(sketch, "E9.113.0", {"start": v(81.72, 74.24) * mm, "mid": v(81.73, 75) * mm, "end": v(81.37, 75.68) * mm});
            skArc(sketch, "E9.113.1", {"start": v(84.94, 71.65) * mm, "mid": v(84.33, 72.08) * mm, "end": v(83.57, 72.16) * mm});
            skArc(sketch, "E9.113.2", {"start": v(81.72, 74.24) * mm, "mid": v(82.07, 72.7) * mm, "end": v(83.57, 72.16) * mm});
            skArc(sketch, "E9.114.0", {"start": v(78.04, 78.1) * mm, "mid": v(78.01, 78.87) * mm, "end": v(77.62, 79.52) * mm});
            skArc(sketch, "E9.114.1", {"start": v(81.38, 75.67) * mm, "mid": v(80.74, 76.07) * mm, "end": v(79.99, 76.11) * mm});
            skArc(sketch, "E9.114.2", {"start": v(78.04, 78.1) * mm, "mid": v(78.47, 76.57) * mm, "end": v(79.99, 76.11) * mm});
            skArc(sketch, "E9.115.0", {"start": v(74.17, 81.78) * mm, "mid": v(74.11, 82.54) * mm, "end": v(73.69, 83.18) * mm});
            skArc(sketch, "E9.115.1", {"start": v(77.63, 79.51) * mm, "mid": v(76.97, 79.88) * mm, "end": v(76.22, 79.89) * mm});
            skArc(sketch, "E9.115.2", {"start": v(74.17, 81.78) * mm, "mid": v(74.67, 80.27) * mm, "end": v(76.22, 79.89) * mm});
            skArc(sketch, "E9.116.0", {"start": v(70.13, 85.27) * mm, "mid": v(70.04, 86.03) * mm, "end": v(69.58, 86.64) * mm});
            skArc(sketch, "E9.116.1", {"start": v(73.7, 83.17) * mm, "mid": v(73.03, 83.51) * mm, "end": v(72.27, 83.48) * mm});
            skArc(sketch, "E9.116.2", {"start": v(70.13, 85.27) * mm, "mid": v(70.7, 83.79) * mm, "end": v(72.27, 83.48) * mm});
            skArc(sketch, "E9.117.0", {"start": v(65.93, 88.56) * mm, "mid": v(65.8, 89.31) * mm, "end": v(65.32, 89.9) * mm});
            skArc(sketch, "E9.117.1", {"start": v(69.6, 86.63) * mm, "mid": v(68.9, 86.94) * mm, "end": v(68.15, 86.87) * mm});
            skArc(sketch, "E9.117.2", {"start": v(65.93, 88.56) * mm, "mid": v(66.58, 87.1) * mm, "end": v(68.15, 86.87) * mm});
            skArc(sketch, "E9.118.0", {"start": v(61.58, 91.64) * mm, "mid": v(61.4, 92.39) * mm, "end": v(60.9, 92.95) * mm});
            skArc(sketch, "E9.118.1", {"start": v(65.33, 89.9) * mm, "mid": v(64.62, 90.17) * mm, "end": v(63.88, 90.06) * mm});
            skArc(sketch, "E9.118.2", {"start": v(61.58, 91.64) * mm, "mid": v(62.3, 90.22) * mm, "end": v(63.88, 90.06) * mm});
            skArc(sketch, "E9.119.0", {"start": v(57.08, 94.51) * mm, "mid": v(56.87, 95.25) * mm, "end": v(56.34, 95.79) * mm});
            skArc(sketch, "E9.119.1", {"start": v(60.9, 92.94) * mm, "mid": v(60.2, 93.19) * mm, "end": v(59.45, 93.04) * mm});
            skArc(sketch, "E9.119.2", {"start": v(57.08, 94.51) * mm, "mid": v(57.86, 93.13) * mm, "end": v(59.45, 93.04) * mm});
            skArc(sketch, "E9.120.0", {"start": v(52.44, 97.16) * mm, "mid": v(52.2, 97.88) * mm, "end": v(51.64, 98.4) * mm});
            skArc(sketch, "E9.120.1", {"start": v(56.35, 95.78) * mm, "mid": v(55.62, 95.98) * mm, "end": v(54.88, 95.8) * mm});
            skArc(sketch, "E9.120.2", {"start": v(52.44, 97.16) * mm, "mid": v(53.3, 95.81) * mm, "end": v(54.88, 95.8) * mm});
            skArc(sketch, "E9.121.0", {"start": v(47.69, 99.58) * mm, "mid": v(47.42, 100.3) * mm, "end": v(46.83, 100.78) * mm});
            skArc(sketch, "E9.121.1", {"start": v(51.66, 98.39) * mm, "mid": v(50.92, 98.56) * mm, "end": v(50.2, 98.34) * mm});
            skArc(sketch, "E9.121.2", {"start": v(47.69, 99.58) * mm, "mid": v(48.6, 98.28) * mm, "end": v(50.2, 98.34) * mm});
            skArc(sketch, "E9.122.0", {"start": v(42.82, 101.77) * mm, "mid": v(42.51, 102.46) * mm, "end": v(41.9, 102.92) * mm});
            skArc(sketch, "E9.122.1", {"start": v(46.84, 100.77) * mm, "mid": v(46.1, 100.9) * mm, "end": v(45.38, 100.65) * mm});
            skArc(sketch, "E9.122.2", {"start": v(42.82, 101.77) * mm, "mid": v(43.8, 100.5) * mm, "end": v(45.38, 100.65) * mm});
            skArc(sketch, "E9.123.0", {"start": v(37.85, 103.72) * mm, "mid": v(37.51, 104.4) * mm, "end": v(36.88, 104.83) * mm});
            skArc(sketch, "E9.123.1", {"start": v(41.92, 102.92) * mm, "mid": v(41.17, 103.01) * mm, "end": v(40.47, 102.73) * mm});
            skArc(sketch, "E9.123.2", {"start": v(37.85, 103.72) * mm, "mid": v(38.9, 102.5) * mm, "end": v(40.47, 102.73) * mm});
            skArc(sketch, "E9.124.0", {"start": v(32.8, 105.42) * mm, "mid": v(32.43, 106.09) * mm, "end": v(31.78, 106.49) * mm});
            skArc(sketch, "E9.124.1", {"start": v(36.9, 104.82) * mm, "mid": v(36.14, 104.88) * mm, "end": v(35.46, 104.56) * mm});
            skArc(sketch, "E9.124.2", {"start": v(32.8, 105.42) * mm, "mid": v(33.9, 104.27) * mm, "end": v(35.46, 104.56) * mm});
            skArc(sketch, "E9.125.0", {"start": v(27.67, 106.89) * mm, "mid": v(27.26, 107.53) * mm, "end": v(26.6, 107.9) * mm});
            skArc(sketch, "E9.125.1", {"start": v(31.79, 106.48) * mm, "mid": v(31.03, 106.5) * mm, "end": v(30.36, 106.16) * mm});
            skArc(sketch, "E9.125.2", {"start": v(27.67, 106.89) * mm, "mid": v(28.82, 105.78) * mm, "end": v(30.36, 106.16) * mm});
            skArc(sketch, "E9.126.0", {"start": v(22.47, 108.1) * mm, "mid": v(22.04, 108.72) * mm, "end": v(21.35, 109.05) * mm});
            skArc(sketch, "E9.126.1", {"start": v(26.6, 107.9) * mm, "mid": v(25.85, 107.88) * mm, "end": v(25.2, 107.5) * mm});
            skArc(sketch, "E9.126.2", {"start": v(22.47, 108.1) * mm, "mid": v(23.67, 107.05) * mm, "end": v(25.2, 107.5) * mm});
            skArc(sketch, "E9.127.0", {"start": v(17.22, 109.06) * mm, "mid": v(16.76, 109.66) * mm, "end": v(16.06, 109.96) * mm});
            skArc(sketch, "E9.127.1", {"start": v(21.36, 109.05) * mm, "mid": v(20.6, 109) * mm, "end": v(19.98, 108.6) * mm});
            skArc(sketch, "E9.127.2", {"start": v(17.22, 109.06) * mm, "mid": v(18.47, 108.07) * mm, "end": v(19.98, 108.6) * mm});
            skArc(sketch, "E9.128.0", {"start": v(11.93, 109.76) * mm, "mid": v(11.44, 110.34) * mm, "end": v(10.73, 110.6) * mm});
            skArc(sketch, "E9.128.1", {"start": v(16.07, 109.96) * mm, "mid": v(15.32, 109.87) * mm, "end": v(14.7, 109.43) * mm});
            skArc(sketch, "E9.128.2", {"start": v(11.93, 109.76) * mm, "mid": v(13.23, 108.84) * mm, "end": v(14.7, 109.43) * mm});
            skArc(sketch, "E9.129.0", {"start": v(6.62, 110.21) * mm, "mid": v(6.1, 110.77) * mm, "end": v(5.37, 111) * mm});
            skArc(sketch, "E9.129.1", {"start": v(10.74, 110.6) * mm, "mid": v(10, 110.48) * mm, "end": v(9.4, 110.01) * mm});
            skArc(sketch, "E9.129.2", {"start": v(6.62, 110.21) * mm, "mid": v(7.95, 109.35) * mm, "end": v(9.4, 110.01) * mm});
            skSolve(sketch);
        }
        {
            var Q0;
            Q0=qSketchRegion(id+"F2",true);
            extrude(context, id + "F3", {"entities" : qUnion([Q0]), "operationType" : NewBodyOperationType.REMOVE, "oppositeDirection" : true, "depth" : 25.4 * mm});
        }
        {
            var Q0;
            Q0=qCreatedBy(makeId("Top.planeOp"),FACE);
            var sketch = newSketch(context, id + "F4", { "sketchPlane" : qUnion([Q0])});
            skCircle(sketch, "E10", {"center": v(0, 0) * mm, "radius": 106.71 * mm});
            skSolve(sketch);
        }
        {
            var Q0;
            Q0=qSketchRegion(id+"F4",true);
            extrude(context, id + "F5", {"entities" : qUnion([Q0]), "depth" : 19.05 * mm, "hasSecondDirection" : true, "secondDirectionOppositeDirection" : true, "secondDirectionDepth" : 6.35 * mm});
        }
        {
            var Q0;
            Q0=makeQuery(id+"F5.opExtrude","CAP_EDGE",EDGE,{"disambiguationData":[OSD([sQuery(id+"F4.wireOp",EDGE,"E10")])],"isStart":false});
            var Q1;
            Q1=makeQuery(id+"F5.opExtrude","CAP_EDGE",EDGE,{"disambiguationData":[OSD([sQuery(id+"F4.wireOp",EDGE,"E10")])],"isStart":true});
            fillet(context, id + "F6", {"entities" : qUnion([Q0, Q1]), "radius" : 6.35 * mm, "tangentPropagation" : true, "allowEdgeOverflow" : false});
        }
        {
            var Q0;
            Q0=makeQuery(id+"F5.opExtrude","SWEPT_BODY",BODY,{"disambiguationData":[OSD([sQuery(id+"F4.wireOp",EDGE,"E10")])]});
            deleteBodies(context, id + "F7", {"entities" : qUnion([Q0])});
        }
        {
            var Q0;
            Q0=qCreatedBy(makeId("Right.planeOp"),FACE);
            var sketch = newSketch(context, id + "F8", { "sketchPlane" : qUnion([Q0])});
            skLineSegment(sketch, "E11", {"start": v(-113.32, 3.36) * mm, "end": v(-113.32, 9.34) * mm});
            skLineSegment(sketch, "E12", {"start": v(-113.32, 9.34) * mm, "end": v(-101.6, 12.7) * mm});
            skLineSegment(sketch, "E13", {"start": v(-101.6, 0) * mm, "end": v(-113.32, 3.36) * mm});
            skLineSegment(sketch, "E14", {"start": v(-101.6, 0) * mm, "end": v(-101.6, 0) * mm});
            skLineSegment(sketch, "E15", {"start": v(-101.6, 0) * mm, "end": v(-119.44, 0) * mm});
            skLineSegment(sketch, "E16", {"start": v(-119.44, 0) * mm, "end": v(-119.44, 12.7) * mm});
            skLineSegment(sketch, "E17", {"start": v(-119.44, 12.7) * mm, "end": v(-101.6, 12.7) * mm});
            skLineSegment(sketch, "E18", {"start": v(0, 0) * mm, "end": v(0, -54.5) * mm, "construction": true});
            skSolve(sketch);
        }
        {
            var Q0;
            Q0=qSketchRegion(id+"F8",true);
            var Q1;
            Q1=sQuery(id+"F8.wireOp",EDGE,"E18");
            revolve(context, id + "F9", {"operationType" : NewBodyOperationType.REMOVE, "entities" : qUnion([Q0]), "axis" : qUnion([Q1]), "revolveType" : RevolveType.FULL, "oppositeDirection" : true});
        }
        {
            var Q0;
            Q0=qCreatedBy(makeId("Top.planeOp"),FACE);
            cPlane(context, id + "F10", {"entities" : qUnion([Q0]), "cplaneType" : CPlaneType.OFFSET, "offset" : 6.35 * mm, "width" : 152.4 * mm, "height" : 152.4 * mm});
        }
        {
            var Q0;
            Q0=qCreatedBy(id+"F10.planeOp",FACE);
            var sketch = newSketch(context, id + "F11", { "sketchPlane" : qUnion([Q0])});
            skPoint(sketch, "E19.center", {"position": v(0, 0) * mm});
            skLineSegment(sketch, "E20", {"start": v(0, 0) * mm, "end": v(0, 111.12) * mm, "construction": true});
            skLineSegment(sketch, "E21", {"start": v(10.73, 110.6) * mm, "end": v(0, 0) * mm, "construction": true});
            skPoint(sketch, "E22.center", {"position": v(-0.2, -0.03) * mm});
            skLineSegment(sketch, "E23", {"start": v(5.3, 109.4) * mm, "end": v(0, 0) * mm, "construction": true});
            skLineSegment(sketch, "E24", {"start": v(0, 109.66) * mm, "end": v(10.6, 109.14) * mm, "construction": true});
            skPoint(sketch, "E25", {"position": v(5.3, 109.4) * mm});
            skLineSegment(sketch, "E26.bottom", {"start": v(1.53, 111.34) * mm, "end": v(9.24, 110.97) * mm});
            skLineSegment(sketch, "E26.left", {"start": v(1.53, 111.34) * mm, "end": v(1.53, 108.58) * mm});
            skLineSegment(sketch, "E26.right", {"start": v(9.24, 110.97) * mm, "end": v(8.97, 108.22) * mm});
            skLineSegment(sketch, "E27", {"start": v(1.53, 108.58) * mm, "end": v(3.34, 107.5) * mm});
            skLineSegment(sketch, "E28", {"start": v(7.06, 107.32) * mm, "end": v(8.97, 108.22) * mm});
            skLineSegment(sketch, "E29", {"start": v(3.34, 107.5) * mm, "end": v(7.06, 107.32) * mm});
            skPoint(sketch, "E30.orphan", {"position": v(5.15, 106.42) * mm});
            skPoint(sketch, "E31", {"position": v(5.2, 107.41) * mm});
            skLineSegment(sketch, "E32.1.0", {"start": v(-3.33, 107.5) * mm, "end": v(-1.52, 108.59) * mm});
            skLineSegment(sketch, "E32.1.1", {"start": v(-9.22, 110.97) * mm, "end": v(-1.52, 111.34) * mm});
            skLineSegment(sketch, "E32.1.2", {"start": v(-9.22, 110.97) * mm, "end": v(-8.96, 108.23) * mm});
            skLineSegment(sketch, "E32.1.3", {"start": v(-7.05, 107.32) * mm, "end": v(-3.33, 107.5) * mm});
            skLineSegment(sketch, "E32.1.4", {"start": v(-1.52, 111.34) * mm, "end": v(-1.52, 108.59) * mm});
            skPoint(sketch, "E32.1.5", {"position": v(-5.19, 107.41) * mm});
            skLineSegment(sketch, "E32.1.6", {"start": v(-8.96, 108.23) * mm, "end": v(-7.05, 107.32) * mm});
            skLineSegment(sketch, "E32.2.0", {"start": v(-13.69, 106.68) * mm, "end": v(-11.99, 107.93) * mm});
            skLineSegment(sketch, "E32.2.1", {"start": v(-19.89, 109.56) * mm, "end": v(-12.26, 110.67) * mm});
            skLineSegment(sketch, "E32.2.2", {"start": v(-19.89, 109.56) * mm, "end": v(-19.36, 106.86) * mm});
            skLineSegment(sketch, "E32.2.3", {"start": v(-17.37, 106.14) * mm, "end": v(-13.69, 106.68) * mm});
            skLineSegment(sketch, "E32.2.4", {"start": v(-12.26, 110.67) * mm, "end": v(-11.99, 107.93) * mm});
            skPoint(sketch, "E32.2.5", {"position": v(-15.53, 106.41) * mm});
            skLineSegment(sketch, "E32.2.6", {"start": v(-19.36, 106.86) * mm, "end": v(-17.37, 106.14) * mm});
            skLineSegment(sketch, "E32.3.0", {"start": v(-23.92, 104.86) * mm, "end": v(-22.35, 106.27) * mm});
            skLineSegment(sketch, "E32.3.1", {"start": v(-30.37, 107.13) * mm, "end": v(-22.88, 108.97) * mm});
            skLineSegment(sketch, "E32.3.2", {"start": v(-30.37, 107.13) * mm, "end": v(-29.58, 104.49) * mm});
            skLineSegment(sketch, "E32.3.3", {"start": v(-27.54, 103.97) * mm, "end": v(-23.92, 104.86) * mm});
            skLineSegment(sketch, "E32.3.4", {"start": v(-22.88, 108.97) * mm, "end": v(-22.35, 106.27) * mm});
            skPoint(sketch, "E32.3.5", {"position": v(-25.73, 104.42) * mm});
            skLineSegment(sketch, "E32.3.6", {"start": v(-29.58, 104.49) * mm, "end": v(-27.54, 103.97) * mm});
            skLineSegment(sketch, "E32.4.0", {"start": v(-33.93, 102.06) * mm, "end": v(-32.5, 103.62) * mm});
            skLineSegment(sketch, "E32.4.1", {"start": v(-40.57, 103.7) * mm, "end": v(-33.3, 106.26) * mm});
            skLineSegment(sketch, "E32.4.2", {"start": v(-40.57, 103.7) * mm, "end": v(-39.53, 101.15) * mm});
            skLineSegment(sketch, "E32.4.3", {"start": v(-37.44, 100.83) * mm, "end": v(-33.93, 102.06) * mm});
            skLineSegment(sketch, "E32.4.4", {"start": v(-33.3, 106.26) * mm, "end": v(-32.5, 103.62) * mm});
            skPoint(sketch, "E32.4.5", {"position": v(-35.69, 101.45) * mm});
            skLineSegment(sketch, "E32.4.6", {"start": v(-39.53, 101.15) * mm, "end": v(-37.44, 100.83) * mm});
            skLineSegment(sketch, "E32.5.0", {"start": v(-43.62, 98.31) * mm, "end": v(-42.35, 100) * mm});
            skLineSegment(sketch, "E32.5.1", {"start": v(-50.39, 99.3) * mm, "end": v(-43.4, 102.55) * mm});
            skLineSegment(sketch, "E32.5.2", {"start": v(-50.39, 99.3) * mm, "end": v(-49.1, 96.86) * mm});
            skLineSegment(sketch, "E32.5.3", {"start": v(-47, 96.74) * mm, "end": v(-43.62, 98.31) * mm});
            skLineSegment(sketch, "E32.5.4", {"start": v(-43.4, 102.55) * mm, "end": v(-42.35, 100) * mm});
            skPoint(sketch, "E32.5.5", {"position": v(-45.31, 97.53) * mm});
            skLineSegment(sketch, "E32.5.6", {"start": v(-49.1, 96.86) * mm, "end": v(-47, 96.74) * mm});
            skLineSegment(sketch, "E32.6.0", {"start": v(-52.9, 93.64) * mm, "end": v(-51.8, 95.44) * mm});
            skLineSegment(sketch, "E32.6.1", {"start": v(-59.73, 93.97) * mm, "end": v(-53.09, 97.88) * mm});
            skLineSegment(sketch, "E32.6.2", {"start": v(-59.73, 93.97) * mm, "end": v(-58.23, 91.67) * mm});
            skLineSegment(sketch, "E32.6.3", {"start": v(-56.12, 91.76) * mm, "end": v(-52.9, 93.64) * mm});
            skLineSegment(sketch, "E32.6.4", {"start": v(-53.09, 97.88) * mm, "end": v(-51.8, 95.44) * mm});
            skPoint(sketch, "E32.6.5", {"position": v(-54.51, 92.7) * mm});
            skLineSegment(sketch, "E32.6.6", {"start": v(-58.23, 91.67) * mm, "end": v(-56.12, 91.76) * mm});
            skLineSegment(sketch, "E32.7.0", {"start": v(-61.7, 88.1) * mm, "end": v(-60.77, 90) * mm});
            skLineSegment(sketch, "E32.7.1", {"start": v(-68.53, 87.77) * mm, "end": v(-62.28, 92.3) * mm});
            skLineSegment(sketch, "E32.7.2", {"start": v(-68.53, 87.77) * mm, "end": v(-66.8, 85.62) * mm});
            skLineSegment(sketch, "E32.7.3", {"start": v(-64.71, 85.91) * mm, "end": v(-61.7, 88.1) * mm});
            skLineSegment(sketch, "E32.7.4", {"start": v(-62.28, 92.3) * mm, "end": v(-60.77, 90) * mm});
            skPoint(sketch, "E32.7.5", {"position": v(-63.2, 87) * mm});
            skLineSegment(sketch, "E32.7.6", {"start": v(-66.8, 85.62) * mm, "end": v(-64.71, 85.91) * mm});
            skLineSegment(sketch, "E32.8.0", {"start": v(-69.91, 81.73) * mm, "end": v(-69.18, 83.71) * mm});
            skLineSegment(sketch, "E32.8.1", {"start": v(-76.68, 80.74) * mm, "end": v(-70.9, 85.86) * mm});
            skLineSegment(sketch, "E32.8.2", {"start": v(-76.68, 80.74) * mm, "end": v(-74.75, 78.77) * mm});
            skLineSegment(sketch, "E32.8.3", {"start": v(-72.7, 79.26) * mm, "end": v(-69.91, 81.73) * mm});
            skLineSegment(sketch, "E32.8.4", {"start": v(-70.9, 85.86) * mm, "end": v(-69.18, 83.71) * mm});
            skPoint(sketch, "E32.8.5", {"position": v(-71.3, 80.5) * mm});
            skLineSegment(sketch, "E32.8.6", {"start": v(-74.75, 78.77) * mm, "end": v(-72.7, 79.26) * mm});
            skLineSegment(sketch, "E32.9.0", {"start": v(-77.47, 74.6) * mm, "end": v(-76.93, 76.64) * mm});
            skLineSegment(sketch, "E32.9.1", {"start": v(-84.11, 72.97) * mm, "end": v(-78.86, 78.61) * mm});
            skLineSegment(sketch, "E32.9.2", {"start": v(-84.11, 72.97) * mm, "end": v(-82, 71.2) * mm});
            skLineSegment(sketch, "E32.9.3", {"start": v(-80.01, 71.88) * mm, "end": v(-77.47, 74.6) * mm});
            skLineSegment(sketch, "E32.9.4", {"start": v(-78.86, 78.61) * mm, "end": v(-76.93, 76.64) * mm});
            skPoint(sketch, "E32.9.5", {"position": v(-78.74, 73.24) * mm});
            skLineSegment(sketch, "E32.9.6", {"start": v(-82, 71.2) * mm, "end": v(-80.01, 71.88) * mm});
            skLineSegment(sketch, "E32.10.0", {"start": v(-84.31, 66.78) * mm, "end": v(-83.97, 68.86) * mm});
            skLineSegment(sketch, "E32.10.1", {"start": v(-90.76, 64.5) * mm, "end": v(-86.08, 70.64) * mm});
            skLineSegment(sketch, "E32.10.2", {"start": v(-90.76, 64.5) * mm, "end": v(-88.5, 62.94) * mm});
            skLineSegment(sketch, "E32.10.3", {"start": v(-86.57, 63.82) * mm, "end": v(-84.31, 66.78) * mm});
            skLineSegment(sketch, "E32.10.4", {"start": v(-86.08, 70.64) * mm, "end": v(-83.97, 68.86) * mm});
            skPoint(sketch, "E32.10.5", {"position": v(-85.44, 65.3) * mm});
            skLineSegment(sketch, "E32.10.6", {"start": v(-88.5, 62.94) * mm, "end": v(-86.57, 63.82) * mm});
            skLineSegment(sketch, "E32.11.0", {"start": v(-90.36, 58.33) * mm, "end": v(-90.23, 60.43) * mm});
            skLineSegment(sketch, "E32.11.1", {"start": v(-96.56, 55.45) * mm, "end": v(-92.5, 62) * mm});
            skLineSegment(sketch, "E32.11.2", {"start": v(-96.56, 55.45) * mm, "end": v(-94.16, 54.1) * mm});
            skLineSegment(sketch, "E32.11.3", {"start": v(-92.33, 55.17) * mm, "end": v(-90.36, 58.33) * mm});
            skLineSegment(sketch, "E32.11.4", {"start": v(-92.5, 62) * mm, "end": v(-90.23, 60.43) * mm});
            skPoint(sketch, "E32.11.5", {"position": v(-91.35, 56.75) * mm});
            skLineSegment(sketch, "E32.11.6", {"start": v(-94.16, 54.1) * mm, "end": v(-92.33, 55.17) * mm});
            skLineSegment(sketch, "E32.12.0", {"start": v(-95.57, 49.34) * mm, "end": v(-95.64, 51.44) * mm});
            skLineSegment(sketch, "E32.12.1", {"start": v(-101.46, 45.87) * mm, "end": v(-98.04, 52.78) * mm});
            skLineSegment(sketch, "E32.12.2", {"start": v(-101.46, 45.87) * mm, "end": v(-98.94, 44.77) * mm});
            skLineSegment(sketch, "E32.12.3", {"start": v(-97.22, 46) * mm, "end": v(-95.57, 49.34) * mm});
            skLineSegment(sketch, "E32.12.4", {"start": v(-98.04, 52.78) * mm, "end": v(-95.64, 51.44) * mm});
            skPoint(sketch, "E32.12.5", {"position": v(-96.4, 47.67) * mm});
            skLineSegment(sketch, "E32.12.6", {"start": v(-98.94, 44.77) * mm, "end": v(-97.22, 46) * mm});
            skLineSegment(sketch, "E32.13.0", {"start": v(-99.89, 39.88) * mm, "end": v(-100.16, 41.97) * mm});
            skLineSegment(sketch, "E32.13.1", {"start": v(-105.42, 35.86) * mm, "end": v(-102.68, 43.07) * mm});
            skLineSegment(sketch, "E32.13.2", {"start": v(-105.42, 35.86) * mm, "end": v(-102.8, 35.01) * mm});
            skLineSegment(sketch, "E32.13.3", {"start": v(-101.2, 36.4) * mm, "end": v(-99.89, 39.88) * mm});
            skLineSegment(sketch, "E32.13.4", {"start": v(-102.68, 43.07) * mm, "end": v(-100.16, 41.97) * mm});
            skPoint(sketch, "E32.13.5", {"position": v(-100.55, 38.14) * mm});
            skLineSegment(sketch, "E32.13.6", {"start": v(-102.8, 35.01) * mm, "end": v(-101.2, 36.4) * mm});
            skLineSegment(sketch, "E32.14.0", {"start": v(-103.27, 30.05) * mm, "end": v(-103.74, 32.11) * mm});
            skLineSegment(sketch, "E32.14.1", {"start": v(-108.39, 25.52) * mm, "end": v(-106.36, 32.96) * mm});
            skLineSegment(sketch, "E32.14.2", {"start": v(-108.39, 25.52) * mm, "end": v(-105.7, 24.93) * mm});
            skLineSegment(sketch, "E32.14.3", {"start": v(-104.25, 26.46) * mm, "end": v(-103.27, 30.05) * mm});
            skLineSegment(sketch, "E32.14.4", {"start": v(-106.36, 32.96) * mm, "end": v(-103.74, 32.11) * mm});
            skPoint(sketch, "E32.14.5", {"position": v(-103.76, 28.26) * mm});
            skLineSegment(sketch, "E32.14.6", {"start": v(-105.7, 24.93) * mm, "end": v(-104.25, 26.46) * mm});
            skLineSegment(sketch, "E32.15.0", {"start": v(-105.69, 19.95) * mm, "end": v(-106.35, 21.95) * mm});
            skLineSegment(sketch, "E32.15.1", {"start": v(-110.34, 14.94) * mm, "end": v(-109.04, 22.54) * mm});
            skLineSegment(sketch, "E32.15.2", {"start": v(-110.34, 14.94) * mm, "end": v(-107.6, 14.6) * mm});
            skLineSegment(sketch, "E32.15.3", {"start": v(-106.32, 16.28) * mm, "end": v(-105.69, 19.95) * mm});
            skLineSegment(sketch, "E32.15.4", {"start": v(-109.04, 22.54) * mm, "end": v(-106.35, 21.95) * mm});
            skPoint(sketch, "E32.15.5", {"position": v(-106, 18.11) * mm});
            skLineSegment(sketch, "E32.15.6", {"start": v(-107.6, 14.6) * mm, "end": v(-106.32, 16.28) * mm});
            skLineSegment(sketch, "E32.16.0", {"start": v(-107.12, 9.65) * mm, "end": v(-107.98, 11.58) * mm});
            skLineSegment(sketch, "E32.16.1", {"start": v(-111.27, 4.22) * mm, "end": v(-110.71, 11.91) * mm});
            skLineSegment(sketch, "E32.16.2", {"start": v(-111.27, 4.22) * mm, "end": v(-108.52, 4.15) * mm});
            skLineSegment(sketch, "E32.16.3", {"start": v(-107.4, 5.94) * mm, "end": v(-107.12, 9.65) * mm});
            skLineSegment(sketch, "E32.16.4", {"start": v(-110.71, 11.91) * mm, "end": v(-107.98, 11.58) * mm});
            skPoint(sketch, "E32.16.5", {"position": v(-107.26, 7.8) * mm});
            skLineSegment(sketch, "E32.16.6", {"start": v(-108.52, 4.15) * mm, "end": v(-107.4, 5.94) * mm});
            skLineSegment(sketch, "E32.17.0", {"start": v(-107.55, -0.73) * mm, "end": v(-108.6, 1.1) * mm});
            skLineSegment(sketch, "E32.17.1", {"start": v(-111.16, -6.54) * mm, "end": v(-111.34, 1.17) * mm});
            skLineSegment(sketch, "E32.17.2", {"start": v(-111.16, -6.54) * mm, "end": v(-108.41, -6.34) * mm});
            skLineSegment(sketch, "E32.17.3", {"start": v(-107.46, -4.45) * mm, "end": v(-107.55, -0.73) * mm});
            skLineSegment(sketch, "E32.17.4", {"start": v(-111.34, 1.17) * mm, "end": v(-108.6, 1.1) * mm});
            skPoint(sketch, "E32.17.5", {"position": v(-107.5, -2.6) * mm});
            skLineSegment(sketch, "E32.17.6", {"start": v(-108.41, -6.34) * mm, "end": v(-107.46, -4.45) * mm});
            skLineSegment(sketch, "E32.18.0", {"start": v(-106.98, -11.1) * mm, "end": v(-108.2, -9.38) * mm});
            skLineSegment(sketch, "E32.18.1", {"start": v(-110, -17.24) * mm, "end": v(-110.94, -9.58) * mm});
            skLineSegment(sketch, "E32.18.2", {"start": v(-110, -17.24) * mm, "end": v(-107.3, -16.77) * mm});
            skLineSegment(sketch, "E32.18.3", {"start": v(-106.53, -14.8) * mm, "end": v(-106.98, -11.1) * mm});
            skLineSegment(sketch, "E32.18.4", {"start": v(-110.94, -9.58) * mm, "end": v(-108.2, -9.38) * mm});
            skPoint(sketch, "E32.18.5", {"position": v(-106.76, -12.96) * mm});
            skLineSegment(sketch, "E32.18.6", {"start": v(-107.3, -16.77) * mm, "end": v(-106.53, -14.8) * mm});
            skLineSegment(sketch, "E32.19.0", {"start": v(-105.4, -21.38) * mm, "end": v(-106.78, -19.78) * mm});
            skLineSegment(sketch, "E32.19.1", {"start": v(-107.83, -27.77) * mm, "end": v(-109.5, -20.24) * mm});
            skLineSegment(sketch, "E32.19.2", {"start": v(-107.83, -27.77) * mm, "end": v(-105.17, -27.05) * mm});
            skLineSegment(sketch, "E32.19.3", {"start": v(-104.6, -25.02) * mm, "end": v(-105.4, -21.38) * mm});
            skLineSegment(sketch, "E32.19.4", {"start": v(-109.5, -20.24) * mm, "end": v(-106.78, -19.78) * mm});
            skPoint(sketch, "E32.19.5", {"position": v(-105, -23.2) * mm});
            skLineSegment(sketch, "E32.19.6", {"start": v(-105.17, -27.05) * mm, "end": v(-104.6, -25.02) * mm});
            skLineSegment(sketch, "E32.20.0", {"start": v(-102.85, -31.45) * mm, "end": v(-104.37, -29.99) * mm});
            skLineSegment(sketch, "E32.20.1", {"start": v(-104.65, -38.05) * mm, "end": v(-107.03, -30.71) * mm});
            skLineSegment(sketch, "E32.20.2", {"start": v(-104.65, -38.05) * mm, "end": v(-102.07, -37.07) * mm});
            skLineSegment(sketch, "E32.20.3", {"start": v(-101.7, -35) * mm, "end": v(-102.85, -31.45) * mm});
            skLineSegment(sketch, "E32.20.4", {"start": v(-107.03, -30.71) * mm, "end": v(-104.37, -29.99) * mm});
            skPoint(sketch, "E32.20.5", {"position": v(-102.28, -33.22) * mm});
            skLineSegment(sketch, "E32.20.6", {"start": v(-102.07, -37.07) * mm, "end": v(-101.7, -35) * mm});
            skLineSegment(sketch, "E32.21.0", {"start": v(-99.34, -41.23) * mm, "end": v(-101, -39.92) * mm});
            skLineSegment(sketch, "E32.21.1", {"start": v(-100.49, -47.97) * mm, "end": v(-103.57, -40.9) * mm});
            skLineSegment(sketch, "E32.21.2", {"start": v(-100.49, -47.97) * mm, "end": v(-98.02, -46.75) * mm});
            skLineSegment(sketch, "E32.21.3", {"start": v(-97.85, -44.65) * mm, "end": v(-99.34, -41.23) * mm});
            skLineSegment(sketch, "E32.21.4", {"start": v(-103.57, -40.9) * mm, "end": v(-101, -39.92) * mm});
            skPoint(sketch, "E32.21.5", {"position": v(-98.6, -42.94) * mm});
            skLineSegment(sketch, "E32.21.6", {"start": v(-98.02, -46.75) * mm, "end": v(-97.85, -44.65) * mm});
            skLineSegment(sketch, "E32.22.0", {"start": v(-94.9, -50.63) * mm, "end": v(-96.67, -49.48) * mm});
            skLineSegment(sketch, "E32.22.1", {"start": v(-95.39, -57.45) * mm, "end": v(-99.14, -50.7) * mm});
            skLineSegment(sketch, "E32.22.2", {"start": v(-95.39, -57.45) * mm, "end": v(-93.05, -56) * mm});
            skLineSegment(sketch, "E32.22.3", {"start": v(-93.08, -53.88) * mm, "end": v(-94.9, -50.63) * mm});
            skLineSegment(sketch, "E32.22.4", {"start": v(-99.14, -50.7) * mm, "end": v(-96.67, -49.48) * mm});
            skPoint(sketch, "E32.22.5", {"position": v(-93.99, -52.26) * mm});
            skLineSegment(sketch, "E32.22.6", {"start": v(-93.05, -56) * mm, "end": v(-93.08, -53.88) * mm});
            skLineSegment(sketch, "E32.23.0", {"start": v(-89.56, -59.55) * mm, "end": v(-91.44, -58.58) * mm});
            skLineSegment(sketch, "E32.23.1", {"start": v(-89.4, -66.38) * mm, "end": v(-93.78, -60.04) * mm});
            skLineSegment(sketch, "E32.23.2", {"start": v(-89.4, -66.38) * mm, "end": v(-87.2, -64.71) * mm});
            skLineSegment(sketch, "E32.23.3", {"start": v(-87.45, -62.62) * mm, "end": v(-89.56, -59.55) * mm});
            skLineSegment(sketch, "E32.23.4", {"start": v(-93.78, -60.04) * mm, "end": v(-91.44, -58.58) * mm});
            skPoint(sketch, "E32.23.5", {"position": v(-88.5, -61.08) * mm});
            skLineSegment(sketch, "E32.23.6", {"start": v(-87.2, -64.71) * mm, "end": v(-87.45, -62.62) * mm});
            skLineSegment(sketch, "E32.24.0", {"start": v(-83.4, -67.92) * mm, "end": v(-85.36, -67.13) * mm});
            skLineSegment(sketch, "E32.24.1", {"start": v(-82.57, -74.7) * mm, "end": v(-87.55, -68.8) * mm});
            skLineSegment(sketch, "E32.24.2", {"start": v(-82.57, -74.7) * mm, "end": v(-80.56, -72.83) * mm});
            skLineSegment(sketch, "E32.24.3", {"start": v(-81, -70.76) * mm, "end": v(-83.4, -67.92) * mm});
            skLineSegment(sketch, "E32.24.4", {"start": v(-87.55, -68.8) * mm, "end": v(-85.36, -67.13) * mm});
            skPoint(sketch, "E32.24.5", {"position": v(-82.2, -69.34) * mm});
            skLineSegment(sketch, "E32.24.6", {"start": v(-80.56, -72.83) * mm, "end": v(-81, -70.76) * mm});
            skLineSegment(sketch, "E32.25.0", {"start": v(-76.45, -75.65) * mm, "end": v(-78.48, -75.06) * mm});
            skLineSegment(sketch, "E32.25.1", {"start": v(-74.98, -82.32) * mm, "end": v(-80.5, -76.93) * mm});
            skLineSegment(sketch, "E32.25.2", {"start": v(-74.98, -82.32) * mm, "end": v(-73.15, -80.26) * mm});
            skLineSegment(sketch, "E32.25.3", {"start": v(-73.79, -78.25) * mm, "end": v(-76.45, -75.65) * mm});
            skLineSegment(sketch, "E32.25.4", {"start": v(-80.5, -76.93) * mm, "end": v(-78.48, -75.06) * mm});
            skPoint(sketch, "E32.25.5", {"position": v(-75.12, -76.95) * mm});
            skLineSegment(sketch, "E32.25.6", {"start": v(-73.15, -80.26) * mm, "end": v(-73.79, -78.25) * mm});
            skLineSegment(sketch, "E32.26.0", {"start": v(-68.8, -82.68) * mm, "end": v(-70.87, -82.28) * mm});
            skLineSegment(sketch, "E32.26.1", {"start": v(-66.68, -89.18) * mm, "end": v(-72.7, -84.34) * mm});
            skLineSegment(sketch, "E32.26.2", {"start": v(-66.68, -89.18) * mm, "end": v(-65.06, -86.95) * mm});
            skLineSegment(sketch, "E32.26.3", {"start": v(-65.9, -85) * mm, "end": v(-68.8, -82.68) * mm});
            skLineSegment(sketch, "E32.26.4", {"start": v(-72.7, -84.34) * mm, "end": v(-70.87, -82.28) * mm});
            skPoint(sketch, "E32.26.5", {"position": v(-67.34, -83.84) * mm});
            skLineSegment(sketch, "E32.26.6", {"start": v(-65.06, -86.95) * mm, "end": v(-65.9, -85) * mm});
            skLineSegment(sketch, "E32.27.0", {"start": v(-60.5, -88.93) * mm, "end": v(-62.6, -88.74) * mm});
            skLineSegment(sketch, "E32.27.1", {"start": v(-57.76, -95.2) * mm, "end": v(-64.22, -90.97) * mm});
            skLineSegment(sketch, "E32.27.2", {"start": v(-57.76, -95.2) * mm, "end": v(-56.37, -92.82) * mm});
            skLineSegment(sketch, "E32.27.3", {"start": v(-57.38, -90.97) * mm, "end": v(-60.5, -88.93) * mm});
            skLineSegment(sketch, "E32.27.4", {"start": v(-64.22, -90.97) * mm, "end": v(-62.6, -88.74) * mm});
            skPoint(sketch, "E32.27.5", {"position": v(-58.94, -89.95) * mm});
            skLineSegment(sketch, "E32.27.6", {"start": v(-56.37, -92.82) * mm, "end": v(-57.38, -90.97) * mm});
            skLineSegment(sketch, "E32.28.0", {"start": v(-51.63, -94.35) * mm, "end": v(-53.74, -94.37) * mm});
            skLineSegment(sketch, "E32.28.1", {"start": v(-48.3, -100.33) * mm, "end": v(-55.14, -96.74) * mm});
            skLineSegment(sketch, "E32.28.2", {"start": v(-48.3, -100.33) * mm, "end": v(-47.15, -97.83) * mm});
            skLineSegment(sketch, "E32.28.3", {"start": v(-48.33, -96.08) * mm, "end": v(-51.63, -94.35) * mm});
            skLineSegment(sketch, "E32.28.4", {"start": v(-55.14, -96.74) * mm, "end": v(-53.74, -94.37) * mm});
            skPoint(sketch, "E32.28.5", {"position": v(-49.98, -95.22) * mm});
            skLineSegment(sketch, "E32.28.6", {"start": v(-47.15, -97.83) * mm, "end": v(-48.33, -96.08) * mm});
            skLineSegment(sketch, "E32.29.0", {"start": v(-42.28, -98.9) * mm, "end": v(-44.38, -99.11) * mm});
            skLineSegment(sketch, "E32.29.1", {"start": v(-38.4, -104.52) * mm, "end": v(-45.54, -101.61) * mm});
            skLineSegment(sketch, "E32.29.2", {"start": v(-38.4, -104.52) * mm, "end": v(-37.48, -101.92) * mm});
            skLineSegment(sketch, "E32.29.3", {"start": v(-38.83, -100.3) * mm, "end": v(-42.28, -98.9) * mm});
            skLineSegment(sketch, "E32.29.4", {"start": v(-45.54, -101.61) * mm, "end": v(-44.38, -99.11) * mm});
            skPoint(sketch, "E32.29.5", {"position": v(-40.56, -99.6) * mm});
            skLineSegment(sketch, "E32.29.6", {"start": v(-37.48, -101.92) * mm, "end": v(-38.83, -100.3) * mm});
            skLineSegment(sketch, "E32.30.0", {"start": v(-32.54, -102.51) * mm, "end": v(-34.6, -102.93) * mm});
            skLineSegment(sketch, "E32.30.1", {"start": v(-28.13, -107.74) * mm, "end": v(-35.52, -105.53) * mm});
            skLineSegment(sketch, "E32.30.2", {"start": v(-28.13, -107.74) * mm, "end": v(-27.47, -105.06) * mm});
            skLineSegment(sketch, "E32.30.3", {"start": v(-28.97, -103.58) * mm, "end": v(-32.54, -102.51) * mm});
            skLineSegment(sketch, "E32.30.4", {"start": v(-35.52, -105.53) * mm, "end": v(-34.6, -102.93) * mm});
            skPoint(sketch, "E32.30.5", {"position": v(-30.76, -103.05) * mm});
            skLineSegment(sketch, "E32.30.6", {"start": v(-27.47, -105.06) * mm, "end": v(-28.97, -103.58) * mm});
            skLineSegment(sketch, "E32.31.0", {"start": v(-22.5, -105.18) * mm, "end": v(-24.51, -105.8) * mm});
            skLineSegment(sketch, "E32.31.1", {"start": v(-17.6, -109.95) * mm, "end": v(-25.17, -108.47) * mm});
            skLineSegment(sketch, "E32.31.2", {"start": v(-17.6, -109.95) * mm, "end": v(-17.2, -107.22) * mm});
            skLineSegment(sketch, "E32.31.3", {"start": v(-18.84, -105.9) * mm, "end": v(-22.5, -105.18) * mm});
            skLineSegment(sketch, "E32.31.4", {"start": v(-25.17, -108.47) * mm, "end": v(-24.51, -105.8) * mm});
            skPoint(sketch, "E32.31.5", {"position": v(-20.67, -105.53) * mm});
            skLineSegment(sketch, "E32.31.6", {"start": v(-17.2, -107.22) * mm, "end": v(-18.84, -105.9) * mm});
            skLineSegment(sketch, "E32.32.0", {"start": v(-12.24, -106.86) * mm, "end": v(-14.19, -107.66) * mm});
            skLineSegment(sketch, "E32.32.1", {"start": v(-6.9, -111.14) * mm, "end": v(-14.59, -110.4) * mm});
            skLineSegment(sketch, "E32.32.2", {"start": v(-6.9, -111.14) * mm, "end": v(-6.78, -108.38) * mm});
            skLineSegment(sketch, "E32.32.3", {"start": v(-8.53, -107.22) * mm, "end": v(-12.24, -106.86) * mm});
            skLineSegment(sketch, "E32.32.4", {"start": v(-14.59, -110.4) * mm, "end": v(-14.19, -107.66) * mm});
            skPoint(sketch, "E32.32.5", {"position": v(-10.39, -107.04) * mm});
            skLineSegment(sketch, "E32.32.6", {"start": v(-6.78, -108.38) * mm, "end": v(-8.53, -107.22) * mm});
            skLineSegment(sketch, "E32.33.0", {"start": v(-1.87, -107.54) * mm, "end": v(-3.73, -108.53) * mm});
            skLineSegment(sketch, "E32.33.1", {"start": v(3.85, -111.28) * mm, "end": v(-3.86, -111.28) * mm});
            skLineSegment(sketch, "E32.33.2", {"start": v(3.85, -111.28) * mm, "end": v(3.72, -108.53) * mm});
            skLineSegment(sketch, "E32.33.3", {"start": v(1.85, -107.54) * mm, "end": v(-1.87, -107.54) * mm});
            skLineSegment(sketch, "E32.33.4", {"start": v(-3.86, -111.28) * mm, "end": v(-3.73, -108.53) * mm});
            skPoint(sketch, "E32.33.5", {"position": v(0, -107.54) * mm});
            skLineSegment(sketch, "E32.33.6", {"start": v(3.72, -108.53) * mm, "end": v(1.85, -107.54) * mm});
            skLineSegment(sketch, "E32.34.0", {"start": v(8.52, -107.22) * mm, "end": v(6.76, -108.39) * mm});
            skLineSegment(sketch, "E32.34.1", {"start": v(14.57, -110.4) * mm, "end": v(6.9, -111.14) * mm});
            skLineSegment(sketch, "E32.34.2", {"start": v(14.57, -110.4) * mm, "end": v(14.17, -107.67) * mm});
            skLineSegment(sketch, "E32.34.3", {"start": v(12.23, -106.86) * mm, "end": v(8.52, -107.22) * mm});
            skLineSegment(sketch, "E32.34.4", {"start": v(6.9, -111.14) * mm, "end": v(6.76, -108.39) * mm});
            skPoint(sketch, "E32.34.5", {"position": v(10.37, -107.04) * mm});
            skLineSegment(sketch, "E32.34.6", {"start": v(14.17, -107.67) * mm, "end": v(12.23, -106.86) * mm});
            skLineSegment(sketch, "E32.35.0", {"start": v(18.83, -105.9) * mm, "end": v(17.2, -107.23) * mm});
            skLineSegment(sketch, "E32.35.1", {"start": v(25.16, -108.47) * mm, "end": v(17.59, -109.95) * mm});
            skLineSegment(sketch, "E32.35.2", {"start": v(25.16, -108.47) * mm, "end": v(24.5, -105.8) * mm});
            skLineSegment(sketch, "E32.35.3", {"start": v(22.48, -105.18) * mm, "end": v(18.83, -105.9) * mm});
            skLineSegment(sketch, "E32.35.4", {"start": v(17.59, -109.95) * mm, "end": v(17.2, -107.23) * mm});
            skPoint(sketch, "E32.35.5", {"position": v(20.65, -105.54) * mm});
            skLineSegment(sketch, "E32.35.6", {"start": v(24.5, -105.8) * mm, "end": v(22.48, -105.18) * mm});
            skLineSegment(sketch, "E32.36.0", {"start": v(28.96, -103.58) * mm, "end": v(27.46, -105.07) * mm});
            skLineSegment(sketch, "E32.36.1", {"start": v(35.5, -105.54) * mm, "end": v(28.12, -107.74) * mm});
            skLineSegment(sketch, "E32.36.2", {"start": v(35.5, -105.54) * mm, "end": v(34.6, -102.94) * mm});
            skLineSegment(sketch, "E32.36.3", {"start": v(32.53, -102.52) * mm, "end": v(28.96, -103.58) * mm});
            skLineSegment(sketch, "E32.36.4", {"start": v(28.12, -107.74) * mm, "end": v(27.46, -105.07) * mm});
            skPoint(sketch, "E32.36.5", {"position": v(30.74, -103.05) * mm});
            skLineSegment(sketch, "E32.36.6", {"start": v(34.6, -102.94) * mm, "end": v(32.53, -102.52) * mm});
            skLineSegment(sketch, "E32.37.0", {"start": v(38.82, -100.3) * mm, "end": v(37.47, -101.93) * mm});
            skLineSegment(sketch, "E32.37.1", {"start": v(45.53, -101.62) * mm, "end": v(38.39, -104.52) * mm});
            skLineSegment(sketch, "E32.37.2", {"start": v(45.53, -101.62) * mm, "end": v(44.37, -99.12) * mm});
            skLineSegment(sketch, "E32.37.3", {"start": v(42.27, -98.9) * mm, "end": v(38.82, -100.3) * mm});
            skLineSegment(sketch, "E32.37.4", {"start": v(38.39, -104.52) * mm, "end": v(37.47, -101.93) * mm});
            skPoint(sketch, "E32.37.5", {"position": v(40.55, -99.6) * mm});
            skLineSegment(sketch, "E32.37.6", {"start": v(44.37, -99.12) * mm, "end": v(42.27, -98.9) * mm});
            skLineSegment(sketch, "E32.38.0", {"start": v(48.32, -96.09) * mm, "end": v(47.13, -97.83) * mm});
            skLineSegment(sketch, "E32.38.1", {"start": v(55.12, -96.75) * mm, "end": v(48.3, -100.33) * mm});
            skLineSegment(sketch, "E32.38.2", {"start": v(55.12, -96.75) * mm, "end": v(53.73, -94.37) * mm});
            skLineSegment(sketch, "E32.38.3", {"start": v(51.62, -94.36) * mm, "end": v(48.32, -96.09) * mm});
            skLineSegment(sketch, "E32.38.4", {"start": v(48.3, -100.33) * mm, "end": v(47.13, -97.83) * mm});
            skPoint(sketch, "E32.38.5", {"position": v(49.97, -95.22) * mm});
            skLineSegment(sketch, "E32.38.6", {"start": v(53.73, -94.37) * mm, "end": v(51.62, -94.36) * mm});
            skLineSegment(sketch, "E32.39.0", {"start": v(57.37, -90.98) * mm, "end": v(56.36, -92.83) * mm});
            skLineSegment(sketch, "E32.39.1", {"start": v(64.2, -90.98) * mm, "end": v(57.75, -95.2) * mm});
            skLineSegment(sketch, "E32.39.2", {"start": v(64.2, -90.98) * mm, "end": v(62.59, -88.75) * mm});
            skLineSegment(sketch, "E32.39.3", {"start": v(60.48, -88.94) * mm, "end": v(57.37, -90.98) * mm});
            skLineSegment(sketch, "E32.39.4", {"start": v(57.75, -95.2) * mm, "end": v(56.36, -92.83) * mm});
            skPoint(sketch, "E32.39.5", {"position": v(58.93, -89.96) * mm});
            skLineSegment(sketch, "E32.39.6", {"start": v(62.59, -88.75) * mm, "end": v(60.48, -88.94) * mm});
            skLineSegment(sketch, "E32.40.0", {"start": v(65.88, -85.02) * mm, "end": v(65.05, -86.96) * mm});
            skLineSegment(sketch, "E32.40.1", {"start": v(72.69, -84.35) * mm, "end": v(66.67, -89.18) * mm});
            skLineSegment(sketch, "E32.40.2", {"start": v(72.69, -84.35) * mm, "end": v(70.86, -82.3) * mm});
            skLineSegment(sketch, "E32.40.3", {"start": v(68.79, -82.68) * mm, "end": v(65.88, -85.02) * mm});
            skLineSegment(sketch, "E32.40.4", {"start": v(66.67, -89.18) * mm, "end": v(65.05, -86.96) * mm});
            skPoint(sketch, "E32.40.5", {"position": v(67.33, -83.85) * mm});
            skLineSegment(sketch, "E32.40.6", {"start": v(70.86, -82.3) * mm, "end": v(68.79, -82.68) * mm});
            skLineSegment(sketch, "E32.41.0", {"start": v(73.78, -78.26) * mm, "end": v(73.14, -80.27) * mm});
            skLineSegment(sketch, "E32.41.1", {"start": v(80.49, -76.95) * mm, "end": v(74.97, -82.33) * mm});
            skLineSegment(sketch, "E32.41.2", {"start": v(80.49, -76.95) * mm, "end": v(78.47, -75.07) * mm});
            skLineSegment(sketch, "E32.41.3", {"start": v(76.44, -75.66) * mm, "end": v(73.78, -78.26) * mm});
            skLineSegment(sketch, "E32.41.4", {"start": v(74.97, -82.33) * mm, "end": v(73.14, -80.27) * mm});
            skPoint(sketch, "E32.41.5", {"position": v(75.11, -76.96) * mm});
            skLineSegment(sketch, "E32.41.6", {"start": v(78.47, -75.07) * mm, "end": v(76.44, -75.66) * mm});
            skLineSegment(sketch, "E32.42.0", {"start": v(80.99, -70.77) * mm, "end": v(80.55, -72.84) * mm});
            skLineSegment(sketch, "E32.42.1", {"start": v(87.54, -68.82) * mm, "end": v(82.56, -74.71) * mm});
            skLineSegment(sketch, "E32.42.2", {"start": v(87.54, -68.82) * mm, "end": v(85.35, -67.15) * mm});
            skLineSegment(sketch, "E32.42.3", {"start": v(83.4, -67.93) * mm, "end": v(80.99, -70.77) * mm});
            skLineSegment(sketch, "E32.42.4", {"start": v(82.56, -74.71) * mm, "end": v(80.55, -72.84) * mm});
            skPoint(sketch, "E32.42.5", {"position": v(82.19, -69.35) * mm});
            skLineSegment(sketch, "E32.42.6", {"start": v(85.35, -67.15) * mm, "end": v(83.4, -67.93) * mm});
            skLineSegment(sketch, "E32.43.0", {"start": v(87.44, -62.63) * mm, "end": v(87.2, -64.72) * mm});
            skLineSegment(sketch, "E32.43.1", {"start": v(93.77, -60.05) * mm, "end": v(89.39, -66.4) * mm});
            skLineSegment(sketch, "E32.43.2", {"start": v(93.77, -60.05) * mm, "end": v(91.43, -58.6) * mm});
            skLineSegment(sketch, "E32.43.3", {"start": v(89.56, -59.56) * mm, "end": v(87.44, -62.63) * mm});
            skLineSegment(sketch, "E32.43.4", {"start": v(89.39, -66.4) * mm, "end": v(87.2, -64.72) * mm});
            skPoint(sketch, "E32.43.5", {"position": v(88.5, -61.1) * mm});
            skLineSegment(sketch, "E32.43.6", {"start": v(91.43, -58.6) * mm, "end": v(89.56, -59.56) * mm});
            skLineSegment(sketch, "E32.44.0", {"start": v(93.08, -53.9) * mm, "end": v(93.04, -56) * mm});
            skLineSegment(sketch, "E32.44.1", {"start": v(99.13, -50.72) * mm, "end": v(95.38, -57.46) * mm});
            skLineSegment(sketch, "E32.44.2", {"start": v(99.13, -50.72) * mm, "end": v(96.66, -49.5) * mm});
            skLineSegment(sketch, "E32.44.3", {"start": v(94.89, -50.64) * mm, "end": v(93.08, -53.9) * mm});
            skLineSegment(sketch, "E32.44.4", {"start": v(95.38, -57.46) * mm, "end": v(93.04, -56) * mm});
            skPoint(sketch, "E32.44.5", {"position": v(93.98, -52.27) * mm});
            skLineSegment(sketch, "E32.44.6", {"start": v(96.66, -49.5) * mm, "end": v(94.89, -50.64) * mm});
            skLineSegment(sketch, "E32.45.0", {"start": v(97.84, -44.66) * mm, "end": v(98.01, -46.76) * mm});
            skLineSegment(sketch, "E32.45.1", {"start": v(103.56, -40.91) * mm, "end": v(100.48, -47.99) * mm});
            skLineSegment(sketch, "E32.45.2", {"start": v(103.56, -40.91) * mm, "end": v(100.99, -39.94) * mm});
            skLineSegment(sketch, "E32.45.3", {"start": v(99.33, -41.25) * mm, "end": v(97.84, -44.66) * mm});
            skLineSegment(sketch, "E32.45.4", {"start": v(100.48, -47.99) * mm, "end": v(98.01, -46.76) * mm});
            skPoint(sketch, "E32.45.5", {"position": v(98.59, -42.95) * mm});
            skLineSegment(sketch, "E32.45.6", {"start": v(100.99, -39.94) * mm, "end": v(99.33, -41.25) * mm});
            skLineSegment(sketch, "E32.46.0", {"start": v(101.7, -35) * mm, "end": v(102.07, -37.09) * mm});
            skLineSegment(sketch, "E32.46.1", {"start": v(107.03, -30.73) * mm, "end": v(104.64, -38.06) * mm});
            skLineSegment(sketch, "E32.46.2", {"start": v(107.03, -30.73) * mm, "end": v(104.37, -30) * mm});
            skLineSegment(sketch, "E32.46.3", {"start": v(102.85, -31.47) * mm, "end": v(101.7, -35) * mm});
            skLineSegment(sketch, "E32.46.4", {"start": v(104.64, -38.06) * mm, "end": v(102.07, -37.09) * mm});
            skPoint(sketch, "E32.46.5", {"position": v(102.27, -33.24) * mm});
            skLineSegment(sketch, "E32.46.6", {"start": v(104.37, -30) * mm, "end": v(102.85, -31.47) * mm});
            skLineSegment(sketch, "E32.47.0", {"start": v(104.6, -25.03) * mm, "end": v(105.17, -27.06) * mm});
            skLineSegment(sketch, "E32.47.1", {"start": v(109.5, -20.25) * mm, "end": v(107.83, -27.79) * mm});
            skLineSegment(sketch, "E32.47.2", {"start": v(109.5, -20.25) * mm, "end": v(106.78, -19.8) * mm});
            skLineSegment(sketch, "E32.47.3", {"start": v(105.4, -21.4) * mm, "end": v(104.6, -25.03) * mm});
            skLineSegment(sketch, "E32.47.4", {"start": v(107.83, -27.79) * mm, "end": v(105.17, -27.06) * mm});
            skPoint(sketch, "E32.47.5", {"position": v(105, -23.21) * mm});
            skLineSegment(sketch, "E32.47.6", {"start": v(106.78, -19.8) * mm, "end": v(105.4, -21.4) * mm});
            skLineSegment(sketch, "E32.48.0", {"start": v(106.53, -14.82) * mm, "end": v(107.3, -16.79) * mm});
            skLineSegment(sketch, "E32.48.1", {"start": v(110.94, -9.6) * mm, "end": v(110, -17.25) * mm});
            skLineSegment(sketch, "E32.48.2", {"start": v(110.94, -9.6) * mm, "end": v(108.19, -9.4) * mm});
            skLineSegment(sketch, "E32.48.3", {"start": v(106.98, -11.12) * mm, "end": v(106.53, -14.82) * mm});
            skLineSegment(sketch, "E32.48.4", {"start": v(110, -17.25) * mm, "end": v(107.3, -16.79) * mm});
            skPoint(sketch, "E32.48.5", {"position": v(106.75, -12.97) * mm});
            skLineSegment(sketch, "E32.48.6", {"start": v(108.19, -9.4) * mm, "end": v(106.98, -11.12) * mm});
            skLineSegment(sketch, "E32.49.0", {"start": v(107.46, -4.47) * mm, "end": v(108.4, -6.35) * mm});
            skLineSegment(sketch, "E32.49.1", {"start": v(111.34, 1.16) * mm, "end": v(111.16, -6.55) * mm});
            skLineSegment(sketch, "E32.49.2", {"start": v(111.34, 1.16) * mm, "end": v(108.6, 1.1) * mm});
            skLineSegment(sketch, "E32.49.3", {"start": v(107.55, -0.74) * mm, "end": v(107.46, -4.47) * mm});
            skLineSegment(sketch, "E32.49.4", {"start": v(111.16, -6.55) * mm, "end": v(108.4, -6.35) * mm});
            skPoint(sketch, "E32.49.5", {"position": v(107.5, -2.6) * mm});
            skLineSegment(sketch, "E32.49.6", {"start": v(108.6, 1.1) * mm, "end": v(107.55, -0.74) * mm});
            skLineSegment(sketch, "E32.50.0", {"start": v(107.4, 5.93) * mm, "end": v(108.52, 4.14) * mm});
            skLineSegment(sketch, "E32.50.1", {"start": v(110.71, 11.9) * mm, "end": v(111.27, 4.2) * mm});
            skLineSegment(sketch, "E32.50.2", {"start": v(110.71, 11.9) * mm, "end": v(107.98, 11.57) * mm});
            skLineSegment(sketch, "E32.50.3", {"start": v(107.12, 9.64) * mm, "end": v(107.4, 5.93) * mm});
            skLineSegment(sketch, "E32.50.4", {"start": v(111.27, 4.2) * mm, "end": v(108.52, 4.14) * mm});
            skPoint(sketch, "E32.50.5", {"position": v(107.26, 7.78) * mm});
            skLineSegment(sketch, "E32.50.6", {"start": v(107.98, 11.57) * mm, "end": v(107.12, 9.64) * mm});
            skLineSegment(sketch, "E32.51.0", {"start": v(106.32, 16.26) * mm, "end": v(107.61, 14.6) * mm});
            skLineSegment(sketch, "E32.51.1", {"start": v(109.05, 22.53) * mm, "end": v(110.34, 14.93) * mm});
            skLineSegment(sketch, "E32.51.2", {"start": v(109.05, 22.53) * mm, "end": v(106.36, 21.94) * mm});
            skLineSegment(sketch, "E32.51.3", {"start": v(105.7, 19.93) * mm, "end": v(106.32, 16.26) * mm});
            skLineSegment(sketch, "E32.51.4", {"start": v(110.34, 14.93) * mm, "end": v(107.61, 14.6) * mm});
            skPoint(sketch, "E32.51.5", {"position": v(106, 18.1) * mm});
            skLineSegment(sketch, "E32.51.6", {"start": v(106.36, 21.94) * mm, "end": v(105.7, 19.93) * mm});
            skLineSegment(sketch, "E32.52.0", {"start": v(104.25, 26.45) * mm, "end": v(105.7, 24.91) * mm});
            skLineSegment(sketch, "E32.52.1", {"start": v(106.36, 32.95) * mm, "end": v(108.39, 25.5) * mm});
            skLineSegment(sketch, "E32.52.2", {"start": v(106.36, 32.95) * mm, "end": v(103.74, 32.1) * mm});
            skLineSegment(sketch, "E32.52.3", {"start": v(103.27, 30.04) * mm, "end": v(104.25, 26.45) * mm});
            skLineSegment(sketch, "E32.52.4", {"start": v(108.39, 25.5) * mm, "end": v(105.7, 24.91) * mm});
            skPoint(sketch, "E32.52.5", {"position": v(103.76, 28.24) * mm});
            skLineSegment(sketch, "E32.52.6", {"start": v(103.74, 32.1) * mm, "end": v(103.27, 30.04) * mm});
            skLineSegment(sketch, "E32.53.0", {"start": v(101.21, 36.39) * mm, "end": v(102.8, 35) * mm});
            skLineSegment(sketch, "E32.53.1", {"start": v(102.69, 43.06) * mm, "end": v(105.42, 35.85) * mm});
            skLineSegment(sketch, "E32.53.2", {"start": v(102.69, 43.06) * mm, "end": v(100.16, 41.96) * mm});
            skLineSegment(sketch, "E32.53.3", {"start": v(99.9, 39.87) * mm, "end": v(101.21, 36.39) * mm});
            skLineSegment(sketch, "E32.53.4", {"start": v(105.42, 35.85) * mm, "end": v(102.8, 35) * mm});
            skPoint(sketch, "E32.53.5", {"position": v(100.55, 38.13) * mm});
            skLineSegment(sketch, "E32.53.6", {"start": v(100.16, 41.96) * mm, "end": v(99.9, 39.87) * mm});
            skLineSegment(sketch, "E32.54.0", {"start": v(97.23, 45.98) * mm, "end": v(98.94, 44.76) * mm});
            skLineSegment(sketch, "E32.54.1", {"start": v(98.05, 52.77) * mm, "end": v(101.47, 45.86) * mm});
            skLineSegment(sketch, "E32.54.2", {"start": v(98.05, 52.77) * mm, "end": v(95.64, 51.43) * mm});
            skLineSegment(sketch, "E32.54.3", {"start": v(95.58, 49.32) * mm, "end": v(97.23, 45.98) * mm});
            skLineSegment(sketch, "E32.54.4", {"start": v(101.47, 45.86) * mm, "end": v(98.94, 44.76) * mm});
            skPoint(sketch, "E32.54.5", {"position": v(96.4, 47.65) * mm});
            skLineSegment(sketch, "E32.54.6", {"start": v(95.64, 51.43) * mm, "end": v(95.58, 49.32) * mm});
            skLineSegment(sketch, "E32.55.0", {"start": v(92.34, 55.15) * mm, "end": v(94.16, 54.1) * mm});
            skLineSegment(sketch, "E32.55.1", {"start": v(92.5, 61.99) * mm, "end": v(96.57, 55.43) * mm});
            skLineSegment(sketch, "E32.55.2", {"start": v(92.5, 61.99) * mm, "end": v(90.23, 60.42) * mm});
            skLineSegment(sketch, "E32.55.3", {"start": v(90.37, 58.32) * mm, "end": v(92.34, 55.15) * mm});
            skLineSegment(sketch, "E32.55.4", {"start": v(96.57, 55.43) * mm, "end": v(94.16, 54.1) * mm});
            skPoint(sketch, "E32.55.5", {"position": v(91.35, 56.74) * mm});
            skLineSegment(sketch, "E32.55.6", {"start": v(90.23, 60.42) * mm, "end": v(90.37, 58.32) * mm});
            skLineSegment(sketch, "E32.56.0", {"start": v(86.58, 63.8) * mm, "end": v(88.5, 62.93) * mm});
            skLineSegment(sketch, "E32.56.1", {"start": v(86.09, 70.63) * mm, "end": v(90.77, 64.5) * mm});
            skLineSegment(sketch, "E32.56.2", {"start": v(86.09, 70.63) * mm, "end": v(83.98, 68.85) * mm});
            skLineSegment(sketch, "E32.56.3", {"start": v(84.32, 66.77) * mm, "end": v(86.58, 63.8) * mm});
            skLineSegment(sketch, "E32.56.4", {"start": v(90.77, 64.5) * mm, "end": v(88.5, 62.93) * mm});
            skPoint(sketch, "E32.56.5", {"position": v(85.45, 65.29) * mm});
            skLineSegment(sketch, "E32.56.6", {"start": v(83.98, 68.85) * mm, "end": v(84.32, 66.77) * mm});
            skLineSegment(sketch, "E32.57.0", {"start": v(80.02, 71.87) * mm, "end": v(82.02, 71.18) * mm});
            skLineSegment(sketch, "E32.57.1", {"start": v(78.87, 78.6) * mm, "end": v(84.12, 72.96) * mm});
            skLineSegment(sketch, "E32.57.2", {"start": v(78.87, 78.6) * mm, "end": v(76.94, 76.63) * mm});
            skLineSegment(sketch, "E32.57.3", {"start": v(77.48, 74.6) * mm, "end": v(80.02, 71.87) * mm});
            skLineSegment(sketch, "E32.57.4", {"start": v(84.12, 72.96) * mm, "end": v(82.02, 71.18) * mm});
            skPoint(sketch, "E32.57.5", {"position": v(78.75, 73.23) * mm});
            skLineSegment(sketch, "E32.57.6", {"start": v(76.94, 76.63) * mm, "end": v(77.48, 74.6) * mm});
            skLineSegment(sketch, "E32.58.0", {"start": v(72.71, 79.25) * mm, "end": v(74.76, 78.76) * mm});
            skLineSegment(sketch, "E32.58.1", {"start": v(70.91, 85.85) * mm, "end": v(76.69, 80.73) * mm});
            skLineSegment(sketch, "E32.58.2", {"start": v(70.91, 85.85) * mm, "end": v(69.19, 83.7) * mm});
            skLineSegment(sketch, "E32.58.3", {"start": v(69.92, 81.72) * mm, "end": v(72.71, 79.25) * mm});
            skLineSegment(sketch, "E32.58.4", {"start": v(76.69, 80.73) * mm, "end": v(74.76, 78.76) * mm});
            skPoint(sketch, "E32.58.5", {"position": v(71.32, 80.49) * mm});
            skLineSegment(sketch, "E32.58.6", {"start": v(69.19, 83.7) * mm, "end": v(69.92, 81.72) * mm});
            skLineSegment(sketch, "E32.59.0", {"start": v(64.72, 85.9) * mm, "end": v(66.81, 85.61) * mm});
            skLineSegment(sketch, "E32.59.1", {"start": v(62.3, 92.3) * mm, "end": v(68.54, 87.76) * mm});
            skLineSegment(sketch, "E32.59.2", {"start": v(62.3, 92.3) * mm, "end": v(60.79, 89.99) * mm});
            skLineSegment(sketch, "E32.59.3", {"start": v(61.7, 88.1) * mm, "end": v(64.72, 85.9) * mm});
            skLineSegment(sketch, "E32.59.4", {"start": v(68.54, 87.76) * mm, "end": v(66.81, 85.61) * mm});
            skPoint(sketch, "E32.59.5", {"position": v(63.22, 87) * mm});
            skLineSegment(sketch, "E32.59.6", {"start": v(60.79, 89.99) * mm, "end": v(61.7, 88.1) * mm});
            skLineSegment(sketch, "E32.60.0", {"start": v(56.13, 91.75) * mm, "end": v(58.24, 91.66) * mm});
            skLineSegment(sketch, "E32.60.1", {"start": v(53.1, 97.87) * mm, "end": v(59.75, 93.96) * mm});
            skLineSegment(sketch, "E32.60.2", {"start": v(53.1, 97.87) * mm, "end": v(51.82, 95.44) * mm});
            skLineSegment(sketch, "E32.60.3", {"start": v(52.92, 93.64) * mm, "end": v(56.13, 91.75) * mm});
            skLineSegment(sketch, "E32.60.4", {"start": v(59.75, 93.96) * mm, "end": v(58.24, 91.66) * mm});
            skPoint(sketch, "E32.60.5", {"position": v(54.52, 92.7) * mm});
            skLineSegment(sketch, "E32.60.6", {"start": v(51.82, 95.44) * mm, "end": v(52.92, 93.64) * mm});
            skLineSegment(sketch, "E32.61.0", {"start": v(47.01, 96.74) * mm, "end": v(49.12, 96.85) * mm});
            skLineSegment(sketch, "E32.61.1", {"start": v(43.4, 102.54) * mm, "end": v(50.4, 99.3) * mm});
            skLineSegment(sketch, "E32.61.2", {"start": v(43.4, 102.54) * mm, "end": v(42.36, 100) * mm});
            skLineSegment(sketch, "E32.61.3", {"start": v(43.63, 98.3) * mm, "end": v(47.01, 96.74) * mm});
            skLineSegment(sketch, "E32.61.4", {"start": v(50.4, 99.3) * mm, "end": v(49.12, 96.85) * mm});
            skPoint(sketch, "E32.61.5", {"position": v(45.32, 97.52) * mm});
            skLineSegment(sketch, "E32.61.6", {"start": v(42.36, 100) * mm, "end": v(43.63, 98.3) * mm});
            skLineSegment(sketch, "E32.62.0", {"start": v(37.46, 100.82) * mm, "end": v(39.54, 101.14) * mm});
            skLineSegment(sketch, "E32.62.1", {"start": v(33.3, 106.25) * mm, "end": v(40.58, 103.7) * mm});
            skLineSegment(sketch, "E32.62.2", {"start": v(33.3, 106.25) * mm, "end": v(32.52, 103.61) * mm});
            skLineSegment(sketch, "E32.62.3", {"start": v(33.94, 102.06) * mm, "end": v(37.46, 100.82) * mm});
            skLineSegment(sketch, "E32.62.4", {"start": v(40.58, 103.7) * mm, "end": v(39.54, 101.14) * mm});
            skPoint(sketch, "E32.62.5", {"position": v(35.7, 101.44) * mm});
            skLineSegment(sketch, "E32.62.6", {"start": v(32.52, 103.61) * mm, "end": v(33.94, 102.06) * mm});
            skLineSegment(sketch, "E32.63.0", {"start": v(27.55, 103.97) * mm, "end": v(29.6, 104.49) * mm});
            skLineSegment(sketch, "E32.63.1", {"start": v(22.9, 108.97) * mm, "end": v(30.38, 107.12) * mm});
            skLineSegment(sketch, "E32.63.2", {"start": v(22.9, 108.97) * mm, "end": v(22.36, 106.27) * mm});
            skLineSegment(sketch, "E32.63.3", {"start": v(23.93, 104.86) * mm, "end": v(27.55, 103.97) * mm});
            skLineSegment(sketch, "E32.63.4", {"start": v(30.38, 107.12) * mm, "end": v(29.6, 104.49) * mm});
            skPoint(sketch, "E32.63.5", {"position": v(25.74, 104.41) * mm});
            skLineSegment(sketch, "E32.63.6", {"start": v(22.36, 106.27) * mm, "end": v(23.93, 104.86) * mm});
            skLineSegment(sketch, "E32.64.0", {"start": v(17.39, 106.14) * mm, "end": v(19.37, 106.85) * mm});
            skLineSegment(sketch, "E32.64.1", {"start": v(12.27, 110.67) * mm, "end": v(19.9, 109.56) * mm});
            skLineSegment(sketch, "E32.64.2", {"start": v(12.27, 110.67) * mm, "end": v(12, 107.93) * mm});
            skLineSegment(sketch, "E32.64.3", {"start": v(13.7, 106.68) * mm, "end": v(17.39, 106.14) * mm});
            skLineSegment(sketch, "E32.64.4", {"start": v(19.9, 109.56) * mm, "end": v(19.37, 106.85) * mm});
            skPoint(sketch, "E32.64.5", {"position": v(15.55, 106.4) * mm});
            skLineSegment(sketch, "E32.64.6", {"start": v(12, 107.93) * mm, "end": v(13.7, 106.68) * mm});
            skSolve(sketch);
        }
        {
            var Q0;
            Q0 = qSketchRegion(id + "F11", true);
            extrude(context, id + "F12", {"entities" : qUnion([Q0]), "operationType" : NewBodyOperationType.REMOVE, "endBound" : BoundingType.THROUGH_ALL, "oppositeDirection" : true, "depth" : 25.4 * mm, "hasSecondDirection" : true, "secondDirectionBound" : SecondDirectionBoundingType.THROUGH_ALL, "secondDirectionOppositeDirection" : false, "secondDirectionDepth" : 25.4 * mm});
        }
    });
